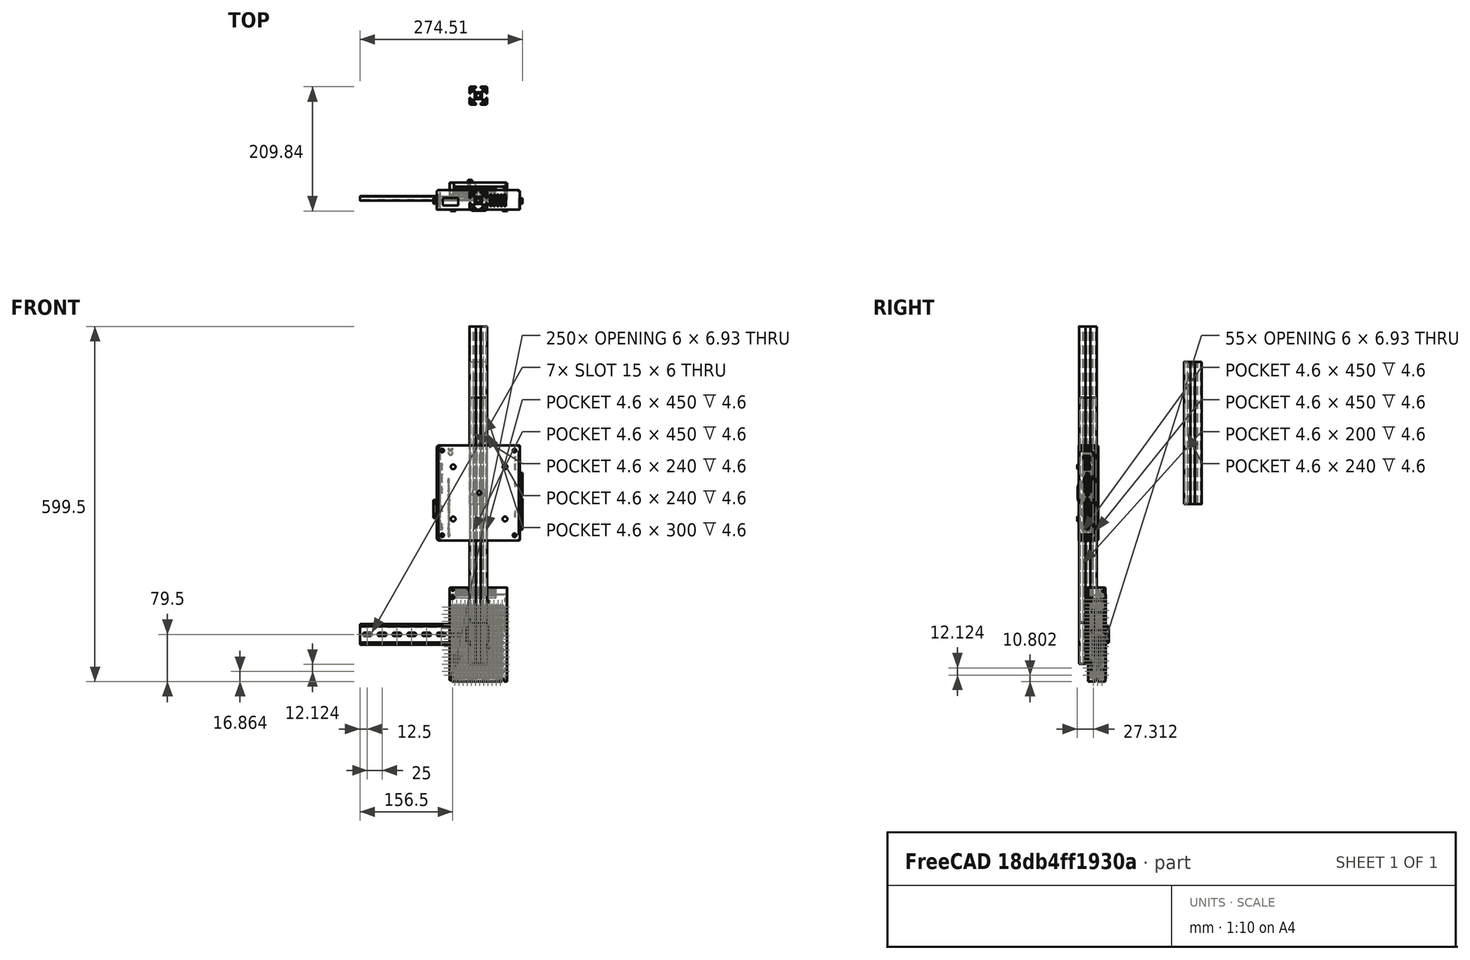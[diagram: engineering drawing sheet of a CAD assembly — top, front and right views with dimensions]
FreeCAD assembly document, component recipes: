
FREECAD ASSEMBLY — COMPONENT RECIPES ("electronics-box")

This assembly document has 40 components, labeled P0..P39 below (a component is one placed body or linked part). 7 of them carry a construction recipe — the FreeCAD feature program that regenerates the part from scratch, quoted from this document or its linked companion documents; the rest are supplied as boundary geometry only. No exploded tour is included for this assembly.
COMPONENT P0 — geometry summary ("LRS-155"; no construction recipe available for this part):
  bounding box: 159.0 x 97.0 x 30.0 mm
  tessellated surface: 57,942 triangles
  volume: 73054 mm^3 (16% of its bounding box)
COMPONENT P1 — geometry summary ("LRS-156"; no construction recipe available for this part):
  bounding box: 159.0 x 97.0 x 30.0 mm
  tessellated surface: 57,942 triangles
  volume: 73054 mm^3 (16% of its bounding box)
COMPONENT P2 — geometry summary ("SMC100CC001"; no construction recipe available for this part):
  bounding box: 161.0 x 150.5 x 35.3 mm
  tessellated surface: 51,434 triangles
  volume: 736162 mm^3 (86% of its bounding box)
COMPONENT P3 — geometry summary ("SMC100CC002"; no construction recipe available for this part):
  bounding box: 161.0 x 150.5 x 35.3 mm
  tessellated surface: 51,434 triangles
  volume: 736162 mm^3 (86% of its bounding box)
COMPONENT P4 — geometry summary ("3030-angle-bracket-001"; no construction recipe available for this part):
  bounding box: 36.7 x 36.7 x 28.0 mm
  tessellated surface: 1,116 triangles
  volume: 10483 mm^3 (28% of its bounding box)
  symmetry: mirror-symmetric across its x mid-plane
COMPONENT P5 — geometry summary ("3030-angle-bracket-002"; no construction recipe available for this part):
  bounding box: 36.7 x 36.7 x 28.0 mm
  tessellated surface: 1,116 triangles
  volume: 10483 mm^3 (28% of its bounding box)
  symmetry: mirror-symmetric across its x mid-plane
COMPONENT P6 — geometry summary ("3030-angle-bracket-003"; no construction recipe available for this part):
  bounding box: 36.7 x 36.7 x 28.0 mm
  tessellated surface: 1,116 triangles
  volume: 10483 mm^3 (28% of its bounding box)
  symmetry: mirror-symmetric across its x mid-plane
COMPONENT P7 — geometry summary ("3030-angle-bracket-004"; no construction recipe available for this part):
  bounding box: 36.7 x 36.7 x 28.0 mm
  tessellated surface: 1,116 triangles
  volume: 10483 mm^3 (28% of its bounding box)
  symmetry: mirror-symmetric across its x mid-plane
COMPONENT P8 — geometry summary ("3030-angle-bracket-005"; no construction recipe available for this part):
  bounding box: 36.7 x 36.7 x 28.0 mm
  tessellated surface: 1,116 triangles
  volume: 10483 mm^3 (28% of its bounding box)
  symmetry: mirror-symmetric across its x mid-plane
COMPONENT P9 — geometry summary ("3030-angle-bracket-006"; no construction recipe available for this part):
  bounding box: 36.7 x 36.7 x 28.0 mm
  tessellated surface: 1,116 triangles
  volume: 10483 mm^3 (28% of its bounding box)
  symmetry: mirror-symmetric across its x mid-plane
COMPONENT P10 — geometry summary ("3030-angle-bracket-007"; no construction recipe available for this part):
  bounding box: 36.7 x 36.7 x 28.0 mm
  tessellated surface: 1,116 triangles
  volume: 10483 mm^3 (28% of its bounding box)
  symmetry: mirror-symmetric across its x mid-plane
COMPONENT P11 — geometry summary ("3030-angle-bracket-008"; no construction recipe available for this part):
  bounding box: 36.7 x 36.7 x 28.0 mm
  tessellated surface: 1,116 triangles
  volume: 10483 mm^3 (28% of its bounding box)
  symmetry: mirror-symmetric across its x mid-plane
COMPONENT P12 — geometry summary ("3030-angle-bracket-009"; no construction recipe available for this part):
  bounding box: 36.7 x 36.7 x 28.0 mm
  tessellated surface: 1,116 triangles
  volume: 10483 mm^3 (28% of its bounding box)
  symmetry: mirror-symmetric across its x mid-plane
COMPONENT P13 — geometry summary ("3030-angle-bracket-010"; no construction recipe available for this part):
  bounding box: 36.7 x 36.7 x 28.0 mm
  tessellated surface: 1,116 triangles
  volume: 10483 mm^3 (28% of its bounding box)
  symmetry: mirror-symmetric across its x mid-plane
COMPONENT P14 — geometry summary ("3030-angle-bracket-011"; no construction recipe available for this part):
  bounding box: 36.7 x 36.7 x 28.0 mm
  tessellated surface: 1,116 triangles
  volume: 10483 mm^3 (28% of its bounding box)
  symmetry: mirror-symmetric across its x mid-plane
COMPONENT P15 — geometry summary ("3030-angle-bracket-012"; no construction recipe available for this part):
  bounding box: 36.7 x 36.7 x 28.0 mm
  tessellated surface: 1,116 triangles
  volume: 10483 mm^3 (28% of its bounding box)
  symmetry: mirror-symmetric across its x mid-plane
COMPONENT P16 — geometry summary ("3030-angle-bracket-013"; no construction recipe available for this part):
  bounding box: 36.7 x 36.7 x 28.0 mm
  tessellated surface: 1,116 triangles
  volume: 10483 mm^3 (28% of its bounding box)
  symmetry: mirror-symmetric across its x mid-plane
COMPONENT P17 — geometry summary ("3030-angle-bracket-014"; no construction recipe available for this part):
  bounding box: 36.7 x 36.7 x 28.0 mm
  tessellated surface: 1,116 triangles
  volume: 10483 mm^3 (28% of its bounding box)
  symmetry: mirror-symmetric across its x mid-plane
COMPONENT P18 — geometry summary ("3030-angle-bracket-015"; no construction recipe available for this part):
  bounding box: 36.7 x 36.7 x 28.0 mm
  tessellated surface: 1,116 triangles
  volume: 10483 mm^3 (28% of its bounding box)
  symmetry: mirror-symmetric across its x mid-plane
COMPONENT P19 — geometry summary ("3030-angle-bracket-016"; no construction recipe available for this part):
  bounding box: 36.7 x 36.7 x 28.0 mm
  tessellated surface: 1,116 triangles
  volume: 10483 mm^3 (28% of its bounding box)
  symmetry: mirror-symmetric across its x mid-plane
COMPONENT P20 — geometry summary ("3030-angle-bracket-017"; no construction recipe available for this part):
  bounding box: 36.7 x 36.7 x 28.0 mm
  tessellated surface: 1,116 triangles
  volume: 10483 mm^3 (28% of its bounding box)
  symmetry: mirror-symmetric across its x mid-plane
COMPONENT P21 — geometry summary ("3030-angle-bracket-018"; no construction recipe available for this part):
  bounding box: 36.7 x 36.7 x 28.0 mm
  tessellated surface: 1,116 triangles
  volume: 10483 mm^3 (28% of its bounding box)
  symmetry: mirror-symmetric across its x mid-plane
COMPONENT P22 — geometry summary ("alu-prof-3030-200-001"; no construction recipe available for this part):
  bounding box: 200.0 x 30.0 x 30.0 mm
  tessellated surface: 1,632 triangles
  volume: 62294 mm^3 (35% of its bounding box)
  symmetry: 2-fold rotationally symmetric about the x axis; 4-fold rotationally symmetric about the y axis; 2-fold rotationally symmetric about the z axis; mirror-symmetric across its x mid-plane, y mid-plane, z mid-plane
COMPONENT P23 — geometry summary ("alu-prof-3030-200-002"; no construction recipe available for this part):
  bounding box: 200.0 x 30.0 x 30.0 mm
  tessellated surface: 1,632 triangles
  volume: 62294 mm^3 (35% of its bounding box)
  symmetry: 2-fold rotationally symmetric about the x axis; 4-fold rotationally symmetric about the y axis; 2-fold rotationally symmetric about the z axis; mirror-symmetric across its x mid-plane, y mid-plane, z mid-plane
COMPONENT P24 — geometry summary ("alu-prof-3030-200-003"; no construction recipe available for this part):
  bounding box: 200.0 x 30.0 x 30.0 mm
  tessellated surface: 1,632 triangles
  volume: 62294 mm^3 (35% of its bounding box)
  symmetry: 2-fold rotationally symmetric about the x axis; 4-fold rotationally symmetric about the y axis; 2-fold rotationally symmetric about the z axis; mirror-symmetric across its x mid-plane, y mid-plane, z mid-plane
COMPONENT P25 — geometry summary ("alu-prof-3030-200-004"; no construction recipe available for this part):
  bounding box: 200.0 x 30.0 x 30.0 mm
  tessellated surface: 1,632 triangles
  volume: 62294 mm^3 (35% of its bounding box)
  symmetry: 2-fold rotationally symmetric about the x axis; 4-fold rotationally symmetric about the y axis; 2-fold rotationally symmetric about the z axis; mirror-symmetric across its x mid-plane, y mid-plane, z mid-plane
COMPONENT P26 — geometry summary ("alu-prof-3030-300-001"; no construction recipe available for this part):
  bounding box: 300.0 x 30.0 x 30.0 mm
  tessellated surface: 1,632 triangles
  volume: 93441 mm^3 (35% of its bounding box)
  symmetry: 2-fold rotationally symmetric about the x axis; 2-fold rotationally symmetric about the y axis; 4-fold rotationally symmetric about the z axis; mirror-symmetric across its x mid-plane, y mid-plane, z mid-plane
COMPONENT P27 — geometry summary ("alu-prof-3030-300-002"; no construction recipe available for this part):
  bounding box: 300.0 x 30.0 x 30.0 mm
  tessellated surface: 1,632 triangles
  volume: 93441 mm^3 (35% of its bounding box)
  symmetry: 2-fold rotationally symmetric about the x axis; 2-fold rotationally symmetric about the y axis; 4-fold rotationally symmetric about the z axis; mirror-symmetric across its x mid-plane, y mid-plane, z mid-plane
COMPONENT P28 — geometry summary ("alu-prof-3030-450-001"; no construction recipe available for this part):
  bounding box: 450.0 x 30.0 x 30.0 mm
  tessellated surface: 1,632 triangles
  volume: 140161 mm^3 (35% of its bounding box)
  symmetry: 4-fold rotationally symmetric about the x axis; 2-fold rotationally symmetric about the y axis; 2-fold rotationally symmetric about the z axis; mirror-symmetric across its x mid-plane, y mid-plane, z mid-plane
COMPONENT P29 — geometry summary ("alu-prof-3030-450-004"; no construction recipe available for this part):
  bounding box: 450.0 x 30.0 x 30.0 mm
  tessellated surface: 1,632 triangles
  volume: 140161 mm^3 (35% of its bounding box)
  symmetry: 4-fold rotationally symmetric about the x axis; 2-fold rotationally symmetric about the y axis; 2-fold rotationally symmetric about the z axis; mirror-symmetric across its x mid-plane, y mid-plane, z mid-plane
COMPONENT P30 — geometry summary ("alu-prof-3030-450-005"; no construction recipe available for this part):
  bounding box: 450.0 x 30.0 x 30.0 mm
  tessellated surface: 1,632 triangles
  volume: 140161 mm^3 (35% of its bounding box)
  symmetry: 4-fold rotationally symmetric about the x axis; 2-fold rotationally symmetric about the y axis; 2-fold rotationally symmetric about the z axis; mirror-symmetric across its x mid-plane, y mid-plane, z mid-plane
COMPONENT P31 — recipe-attached ("din_mount_part", a linked part whose construction recipe lives in a companion FreeCAD document of the same project; that document's serialized recipe follows).
Construction recipe (the companion document, serialized — sketch geometry with constraints, then the solid features built on it; lengths are millimeters unless a unit is written):

FCSTD DOCUMENT  (FreeCAD 1.0R39285 (Git))
Label: din_mount
License: All rights reserved
objects: Sketcher::SketchObject×4, PartDesign::Pad×2, PartDesign::Pocket×2, PartDesign::Chamfer×1, PartDesign::Body×1, App::Part×1
note: 24 computed .brp shape members not serialized (recipe doc carries the construction recipe); baked Part::Feature solids carry a one-line shape summary decoded from their .brp

FEATURE [Sketcher::SketchObject] Sketch
  ArcFitTolerance = 1e-06
  AttachmentSupport = -> [XY_Plane]
  FullyConstrained = true
  MakeInternals = false
  MapMode = 5
  expr: Constraints[33] = 10
  sketch-geometry (17):
    g0: LineSegment StartX=-17.9289 StartY=-15 StartZ=0 EndX=17.9289 EndY=-15 EndZ=0
    g1: LineSegment StartX=25 StartY=-7.92893 StartZ=0 EndX=25 EndY=7.92893 EndZ=0
    g2: LineSegment StartX=17.9289 StartY=15 StartZ=0 EndX=-17.9289 EndY=15 EndZ=0
    g3: LineSegment StartX=-25 StartY=7.92893 StartZ=0 EndX=-25 EndY=-7.92893 EndZ=0
    g4: GeomPoint [constr] X=0 Y=0 Z=0
    g5: ArcOfCircle [constr] CenterX=-17.9289 CenterY=7.92893 CenterZ=0 NormalX=0 NormalY=0 NormalZ=1 AngleXU=0 Radius=7.07107 StartAngle=1.5708 EndAngle=3.14159
    g6: GeomPoint [constr] X=-25 Y=15 Z=0
    g7: LineSegment StartX=-17.9289 StartY=15 StartZ=0 EndX=-25 EndY=7.92893 EndZ=0
    g8: ArcOfCircle [constr] CenterX=17.9289 CenterY=7.92893 CenterZ=0 NormalX=0 NormalY=0 NormalZ=1 AngleXU=0 Radius=7.07107 StartAngle=1e-16 EndAngle=1.5708
    g9: GeomPoint [constr] X=25 Y=15 Z=0
    g10: LineSegment StartX=25 StartY=7.92893 StartZ=0 EndX=17.9289 EndY=15 EndZ=0
    g11: ArcOfCircle [constr] CenterX=17.9289 CenterY=-7.92893 CenterZ=0 NormalX=0 NormalY=0 NormalZ=1 AngleXU=0 Radius=7.07107 StartAngle=4.71239 EndAngle=6.28319
    g12: GeomPoint [constr] X=25 Y=-15 Z=0
    g13: LineSegment StartX=17.9289 StartY=-15 StartZ=0 EndX=25 EndY=-7.92893 EndZ=0
    g14: ArcOfCircle [constr] CenterX=-17.9289 CenterY=-7.92893 CenterZ=0 NormalX=0 NormalY=0 NormalZ=1 AngleXU=0 Radius=7.07107 StartAngle=3.14159 EndAngle=4.71239
    g15: GeomPoint [constr] X=-25 Y=-15 Z=0
    g16: LineSegment StartX=-25 StartY=-7.92893 StartZ=0 EndX=-17.9289 EndY=-15 EndZ=0
  constraints (36):
    c: Horizontal(g0)
    c: Horizontal(g2)
    c: Vertical(g1)
    c: Vertical(g3)
    c: Symmetric(g9,g15,g4)
    c: Distance(g12,g15) = 50
    c: Distance(g15,g6) = 30
    c: Coincident(g4,g-1)
    c: PointOnObject(g6,g2)
    c: PointOnObject(g6,g3)
    c: Tangent(g2,g5) = -1.5708
    c: Tangent(g3,g5) = -1.5708
    c: Coincident(g7,g2)
    c: Coincident(g7,g3)
    c: PointOnObject(g9,g2)
    c: PointOnObject(g9,g1)
    c: Tangent(g2,g8) = -1.5708
    c: Tangent(g1,g8) = -1.5708
    c: Coincident(g10,g2)
    c: Coincident(g10,g1)
    c: PointOnObject(g12,g0)
    c: PointOnObject(g12,g1)
    c: Tangent(g0,g11) = -1.5708
    c: Tangent(g1,g11) = -1.5708
    c: Coincident(g13,g0)
    c: Coincident(g13,g1)
    c: PointOnObject(g15,g3)
    c: PointOnObject(g15,g0)
    c: Tangent(g3,g14) = -1.5708
    c: Tangent(g0,g14) = -1.5708
    c: Coincident(g16,g3)
    c: Coincident(g16,g0)
    c: Distance(g7,g7) = 10
    c: Distance(g10,g10) = 10
    c: Distance(g13,g13) = 10
    c: Distance(g16,g16) = 10
FEATURE [PartDesign::Pad] Pad
  Direction = (0,0,1)
  Length = 5
  Length2 = 10
  Profile = -> Sketch
  ReferenceAxis = -> Sketch [N_Axis]
  Refine = true
  Suppressed = false
  Type = 0
FEATURE [Sketcher::SketchObject] Sketch001
  ArcFitTolerance = 1e-06
  AttachmentSupport = -> [YZ_Plane]
  FullyConstrained = true
  MakeInternals = false
  MapMode = 5
  Placement = pos=(0,0,0) rot=(0.57735,0.57735,0.57735;2.0944rad)
  sketch-geometry (6):
    g0: LineSegment StartX=0 StartY=0 StartZ=0 EndX=-10 EndY=0 EndZ=0
    g1: LineSegment StartX=-10 StartY=0 StartZ=0 EndX=-10 EndY=15 EndZ=0
    g2: LineSegment StartX=0 StartY=0 StartZ=0 EndX=15 EndY=0 EndZ=0
    g3: LineSegment StartX=15 StartY=0 StartZ=0 EndX=15 EndY=60 EndZ=0
    g4: LineSegment StartX=15 StartY=60 StartZ=0 EndX=3 EndY=60 EndZ=0
    g5: LineSegment StartX=3 StartY=60 StartZ=0 EndX=-10 EndY=15 EndZ=0
  constraints (17):
    c: Distance(g0) = 10
    c: Coincident(g0,g-1)
    c: PointOnObject(g0,g-1)
    c: Distance(g1) = 15
    c: Coincident(g1,g0)
    c: Vertical(g1)
    c: Distance(g2) = 15
    c: Coincident(g2,g0)
    c: PointOnObject(g2,g-1)
    c: Distance(g3) = 60
    c: Coincident(g3,g2)
    c: Vertical(g3)
    c: Distance(g4) = 12
    c: Coincident(g4,g3)
    c: Horizontal(g4)
    c: Coincident(g5,g4)
    c: Coincident(g5,g1)
FEATURE [PartDesign::Pad] Pad001
  BaseFeature = -> Pad
  Direction = (1,0,0)
  Length = 15
  Length2 = 10
  Midplane = true
  Profile = -> Sketch001
  ReferenceAxis = -> Sketch001 [N_Axis]
  Refine = true
  Suppressed = false
  Type = 0
FEATURE [PartDesign::Chamfer] Chamfer
  Angle = 45
  Base = -> Pad001 [Edge37,Edge34,Edge29,Edge28,Edge33,Edge35,Edge30]
  BaseFeature = -> Pad001
  ChamferType = 0
  FlipDirection = false
  Refine = true
  Size = 2.5
  Size2 = 1
  SupportTransform = false
  Suppressed = false
  UseAllEdges = false
FEATURE [Sketcher::SketchObject] Sketch002
  ArcFitTolerance = 1e-06
  AttachmentSupport = -> [Chamfer]
  FullyConstrained = true
  MakeInternals = false
  MapMode = 5
  Placement = pos=(0,15,0) rot=(0,0.707107,0.707107;3.14159rad)
  sketch-geometry (2):
    g0: LineSegment [constr] StartX=0 StartY=0 StartZ=0 EndX=0 EndY=52.5 EndZ=0
    g1: Circle CenterX=0 CenterY=52.5 CenterZ=0 NormalX=0 NormalY=0 NormalZ=1 AngleXU=0 Radius=3.25
  constraints (5):
    c: Distance(g0) = 52.5
    c: Coincident(g0,g-1)
    c: Vertical(g0)
    c: Diameter(g1) = 6.5
    c: Coincident(g1,g0)
FEATURE [PartDesign::Pocket] Pocket
  BaseFeature = -> Chamfer
  Direction = (0,-1,2e-16)
  Length = 11
  Length2 = 5
  Profile = -> Sketch002
  ReferenceAxis = -> Sketch002 [N_Axis]
  Refine = true
  Suppressed = false
  Type = 0
FEATURE [Sketcher::SketchObject] Sketch003
  ArcFitTolerance = 1e-06
  AttachmentSupport = -> [Pocket]
  FullyConstrained = true
  MakeInternals = false
  MapMode = 5
  Placement = pos=(0,0,0) rot=(1,0,0;3.14159rad)
  sketch-geometry (4):
    g0: LineSegment [constr] StartX=0 StartY=0 StartZ=0 EndX=16 EndY=0 EndZ=0
    g1: LineSegment [constr] StartX=0 StartY=0 StartZ=0 EndX=-16 EndY=0 EndZ=0
    g2: Circle CenterX=-16 CenterY=0 CenterZ=0 NormalX=0 NormalY=0 NormalZ=1 AngleXU=0 Radius=2.6
    g3: Circle CenterX=16 CenterY=0 CenterZ=0 NormalX=0 NormalY=0 NormalZ=1 AngleXU=0 Radius=2.6
  constraints (10):
    c: Distance(g0) = 16
    c: Coincident(g0,g-1)
    c: PointOnObject(g0,g-1)
    c: Distance(g1) = 16
    c: Coincident(g1,g0)
    c: PointOnObject(g1,g-1)
    c: Diameter(g2) = 5.2
    c: Coincident(g2,g1)
    c: Diameter(g3) = 5.2
    c: Coincident(g3,g0)
FEATURE [PartDesign::Pocket] Pocket001
  BaseFeature = -> Pocket
  Direction = (0,0,1)
  Length = 5
  Length2 = 5
  Profile = -> Sketch003
  ReferenceAxis = -> Sketch003 [N_Axis]
  Refine = true
  Suppressed = false
  Type = 0
FEATURE [PartDesign::Body] Body  label="din_mount_body"
  AllowCompound = false
  Group = -> [Sketch,Pad,Sketch001,Pad001,Chamfer,Sketch002,Pocket,Sketch003,Pocket001]
  Origin = -> Origin
  Tip = -> Pocket001
FEATURE [App::Part] Part  label="din_mount_part"
  Group = -> [Body]
  Origin = -> Origin001
COMPONENT P32 — same part as P31; its construction recipe is shown at P31.
COMPONENT P33 — geometry summary ("din_rail_180mm001"; no construction recipe available for this part):
  bounding box: 180.0 x 35.0 x 7.5 mm
  tessellated surface: 2,968 triangles
  volume: 7678 mm^3 (16% of its bounding box)
  symmetry: mirror-symmetric across its z mid-plane
COMPONENT P34 — geometry summary ("dlp-power-supply-bracket-part"; no construction recipe available for this part):
  bounding box: 130.0 x 73.0 x 71.0 mm
  tessellated surface: 504 triangles
  volume: 33959 mm^3 (5% of its bounding box)
  symmetry: mirror-symmetric across its x mid-plane
COMPONENT P35 — recipe-attached ("ports-panel-part", a linked part whose construction recipe lives in a companion FreeCAD document of the same project; that document's serialized recipe follows).
Construction recipe (the companion document, serialized — sketch geometry with constraints, then the solid features built on it; lengths are millimeters unless a unit is written):

FCSTD DOCUMENT  (FreeCAD 1.0R39319 (Git))
Label: ports-panel
License: All rights reserved
objects: Sketcher::SketchObject×9, PartDesign::Pocket×7, PartDesign::Pad×2, PartDesign::Chamfer×2, PartDesign::Body×1, App::Part×1
note: 52 computed .brp shape members not serialized (recipe doc carries the construction recipe); baked Part::Feature solids carry a one-line shape summary decoded from their .brp

FEATURE [Sketcher::SketchObject] Sketch
  ArcFitTolerance = 1e-06
  AttachmentSupport = -> [XY_Plane]
  FullyConstrained = true
  MakeInternals = false
  MapMode = 5
  sketch-geometry (5):
    g0: LineSegment StartX=-115 StartY=-37.5 StartZ=0 EndX=115 EndY=-37.5 EndZ=0
    g1: LineSegment StartX=115 StartY=-37.5 StartZ=0 EndX=115 EndY=37.5 EndZ=0
    g2: LineSegment StartX=115 StartY=37.5 StartZ=0 EndX=-115 EndY=37.5 EndZ=0
    g3: LineSegment StartX=-115 StartY=37.5 StartZ=0 EndX=-115 EndY=-37.5 EndZ=0
    g4: GeomPoint [constr] X=0 Y=-1e-16 Z=0
  constraints (12):
    c: Coincident(g0,g1)
    c: Coincident(g1,g2)
    c: Coincident(g2,g3)
    c: Coincident(g3,g0)
    c: Horizontal(g0)
    c: Horizontal(g2)
    c: Vertical(g1)
    c: Vertical(g3)
    c: Symmetric(g2,g0,g4)
    c: Distance(g1,g3) = 230
    c: Distance(g0,g2) = 75
    c: Coincident(g4,g-1)
FEATURE [PartDesign::Pad] Pad
  Direction = (0,0,1)
  Length = 6.2
  Length2 = 10
  Profile = -> Sketch
  ReferenceAxis = -> Sketch [N_Axis]
  Refine = true
  Suppressed = false
  Type = 0
FEATURE [Sketcher::SketchObject] Sketch001
  ArcFitTolerance = 1e-06
  AttachmentSupport = -> [Pad]
  FullyConstrained = true
  MakeInternals = false
  MapMode = 5
  Placement = pos=(0,0,6.2) rot=(0,0,1;0rad)
  sketch-geometry (9):
    g0: LineSegment [constr] StartX=-115 StartY=-37.5 StartZ=0 EndX=115 EndY=-37.5 EndZ=0
    g1: LineSegment [constr] StartX=115 StartY=-37.5 StartZ=0 EndX=115 EndY=37.5 EndZ=0
    g2: LineSegment [constr] StartX=115 StartY=37.5 StartZ=0 EndX=-115 EndY=37.5 EndZ=0
    g3: LineSegment [constr] StartX=-115 StartY=37.5 StartZ=0 EndX=-115 EndY=-37.5 EndZ=0
    g4: GeomPoint [constr] X=0 Y=0 Z=0
    g5: LineSegment StartX=115 StartY=37.5 StartZ=0 EndX=-96 EndY=37.5 EndZ=0
    g6: LineSegment StartX=-96 StartY=37.5 StartZ=0 EndX=-96 EndY=33.5 EndZ=0
    g7: LineSegment StartX=-96 StartY=33.5 StartZ=0 EndX=115 EndY=33.5 EndZ=0
    g8: LineSegment StartX=115 StartY=33.5 StartZ=0 EndX=115 EndY=37.5 EndZ=0
  constraints (23):
    c: Coincident(g0,g1)
    c: Coincident(g1,g2)
    c: Coincident(g2,g3)
    c: Coincident(g3,g0)
    c: Horizontal(g0)
    c: Horizontal(g2)
    c: Vertical(g1)
    c: Vertical(g3)
    c: Symmetric(g2,g0,g4)
    c: Distance(g1,g3) = 230
    c: Distance(g0,g2) = 75
    c: Coincident(g4,g-1)
    c: Coincident(g5,g6)
    c: Coincident(g6,g7)
    c: Coincident(g7,g8)
    c: Coincident(g8,g5)
    c: Horizontal(g5)
    c: Horizontal(g7)
    c: Vertical(g6)
    c: Vertical(g8)
    c: Distance(g6,g8) = 211
    c: Distance(g5,g7) = 4
    c: Coincident(g5,g1)
FEATURE [PartDesign::Pocket] Pocket
  BaseFeature = -> Pad
  Direction = (0,0,-1)
  Length = 3.2
  Length2 = 5
  Profile = -> Sketch001
  ReferenceAxis = -> Sketch001 [N_Axis]
  Refine = true
  Suppressed = false
  Type = 0
FEATURE [PartDesign::Chamfer] Chamfer
  Angle = 45
  Base = -> Pocket [Edge6,Edge3,Edge8]
  BaseFeature = -> Pocket
  ChamferType = 0
  FlipDirection = false
  Refine = true
  Size = 2
  Size2 = 1
  SupportTransform = false
  Suppressed = false
  UseAllEdges = false
FEATURE [Sketcher::SketchObject] Sketch002
  ArcFitTolerance = 1e-06
  AttachmentSupport = -> [Chamfer]
  FullyConstrained = true
  MakeInternals = false
  MapMode = 5
  Placement = pos=(0,0,6.2) rot=(0,0,1;0rad)
  sketch-geometry (9):
    g0: LineSegment [constr] StartX=-100 StartY=-22.5 StartZ=0 EndX=100 EndY=-22.5 EndZ=0
    g1: LineSegment [constr] StartX=100 StartY=-22.5 StartZ=0 EndX=100 EndY=22.5 EndZ=0
    g2: LineSegment [constr] StartX=100 StartY=22.5 StartZ=0 EndX=-100 EndY=22.5 EndZ=0
    g3: LineSegment [constr] StartX=-100 StartY=22.5 StartZ=0 EndX=-100 EndY=-22.5 EndZ=0
    g4: GeomPoint [constr] X=0 Y=0 Z=0
    g5: Circle CenterX=-100 CenterY=-22.5 CenterZ=0 NormalX=0 NormalY=0 NormalZ=1 AngleXU=0 Radius=2.6
    g6: Circle CenterX=0 CenterY=-22.5 CenterZ=0 NormalX=0 NormalY=0 NormalZ=1 AngleXU=0 Radius=2.6
    g7: Circle CenterX=100 CenterY=-22.5 CenterZ=0 NormalX=0 NormalY=0 NormalZ=1 AngleXU=0 Radius=2.6
    g8: Circle CenterX=-100 CenterY=22.5 CenterZ=0 NormalX=0 NormalY=0 NormalZ=1 AngleXU=0 Radius=2.6
  constraints (20):
    c: Coincident(g0,g1)
    c: Coincident(g1,g2)
    c: Coincident(g2,g3)
    c: Coincident(g3,g0)
    c: Horizontal(g0)
    c: Horizontal(g2)
    c: Vertical(g1)
    c: Vertical(g3)
    c: Symmetric(g2,g0,g4)
    c: Distance(g1,g3) = 200
    c: Distance(g0,g2) = 45
    c: Coincident(g4,g-1)
    c: Diameter(g5) = 5.2
    c: Coincident(g5,g0)
    c: Diameter(g6) = 5.2
    c: Symmetric(g0,g0,g6)
    c: Diameter(g7) = 5.2
    c: Coincident(g7,g0)
    c: Diameter(g8) = 5.2
    c: Coincident(g8,g2)
FEATURE [PartDesign::Pocket] Pocket001
  BaseFeature = -> Chamfer
  Direction = (0,0,-1)
  Length = 10
  Length2 = 5
  Profile = -> Sketch002
  ReferenceAxis = -> Sketch002 [N_Axis]
  Refine = true
  Suppressed = false
  Type = 0
FEATURE [Sketcher::SketchObject] Sketch003
  ArcFitTolerance = 1e-06
  AttachmentSupport = -> [Pocket001]
  FullyConstrained = true
  MakeInternals = false
  MapMode = 5
  Placement = pos=(0,0,0) rot=(1,0,0;3.14159rad)
  sketch-geometry (17):
    g0: LineSegment [constr] StartX=-115 StartY=-37.5 StartZ=0 EndX=115 EndY=-37.5 EndZ=0
    g1: LineSegment [constr] StartX=115 StartY=-37.5 StartZ=0 EndX=115 EndY=37.5 EndZ=0
    g2: LineSegment [constr] StartX=115 StartY=37.5 StartZ=0 EndX=-115 EndY=37.5 EndZ=0
    g3: LineSegment [constr] StartX=-115 StartY=37.5 StartZ=0 EndX=-115 EndY=-37.5 EndZ=0
    g4: GeomPoint [constr] X=0 Y=0 Z=0
    g5: LineSegment [constr] StartX=115 StartY=37.5 StartZ=0 EndX=-115 EndY=37.5 EndZ=0
    g6: LineSegment [constr] StartX=-115 StartY=37.5 StartZ=0 EndX=-115 EndY=7.5 EndZ=0
    g7: LineSegment [constr] StartX=-115 StartY=7.5 StartZ=0 EndX=115 EndY=7.5 EndZ=0
    g8: LineSegment [constr] StartX=115 StartY=7.5 StartZ=0 EndX=115 EndY=37.5 EndZ=0
    g9: LineSegment [constr] StartX=0 StartY=0 StartZ=0 EndX=0 EndY=-1 EndZ=0
    g10: LineSegment [constr] StartX=0 StartY=-1 StartZ=0 EndX=20 EndY=-1 EndZ=0
    g11: LineSegment [constr] StartX=20 StartY=-1 StartZ=0 EndX=20 EndY=0 EndZ=0
    g12: LineSegment [constr] StartX=20 StartY=0 StartZ=0 EndX=0 EndY=0 EndZ=0
    g13: LineSegment StartX=20 StartY=-1 StartZ=0 EndX=20 EndY=-28.2 EndZ=0
    g14: LineSegment StartX=20 StartY=-28.2 StartZ=0 EndX=67.4 EndY=-28.2 EndZ=0
    g15: LineSegment StartX=67.4 StartY=-28.2 StartZ=0 EndX=67.4 EndY=-1 EndZ=0
    g16: LineSegment StartX=67.4 StartY=-1 StartZ=0 EndX=20 EndY=-1 EndZ=0
  constraints (45):
    c: Coincident(g0,g1)
    c: Coincident(g1,g2)
    c: Coincident(g2,g3)
    c: Coincident(g3,g0)
    c: Horizontal(g0)
    c: Horizontal(g2)
    c: Vertical(g1)
    c: Vertical(g3)
    c: Symmetric(g2,g0,g4)
    c: Distance(g1,g3) = 230
    c: Distance(g0,g2) = 75
    c: Coincident(g4,g-1)
    c: Coincident(g5,g6)
    c: Coincident(g6,g7)
    c: Coincident(g7,g8)
    c: Coincident(g8,g5)
    c: Horizontal(g5)
    c: Horizontal(g7)
    c: Vertical(g6)
    c: Vertical(g8)
    c: Distance(g5,g7) = 30
    c: Coincident(g5,g1)
    c: PointOnObject(g6,g3)
    c: Coincident(g9,g10)
    c: Coincident(g10,g11)
    c: Coincident(g11,g12)
    c: Coincident(g12,g9)
    c: Vertical(g9)
    c: Vertical(g11)
    c: Horizontal(g10)
    c: Horizontal(g12)
    c: Distance(g9,g11) = 20
    c: Distance(g10,g12) = 1
    c: Coincident(g9,g4)
    c: Coincident(g13,g14)
    c: Coincident(g14,g15)
    c: Coincident(g15,g16)
    c: Coincident(g16,g13)
    c: Vertical(g13)
    c: Vertical(g15)
    c: Horizontal(g14)
    c: Horizontal(g16)
    c: Distance(g13,g15) = 47.4
    c: Distance(g14,g16) = 27.2
    c: Coincident(g13,g10)
FEATURE [PartDesign::Pocket] Pocket002
  BaseFeature = -> Pocket001
  Direction = (0,0,1)
  Length = 7
  Length2 = 5
  Profile = -> Sketch003
  ReferenceAxis = -> Sketch003 [N_Axis]
  Refine = true
  Suppressed = false
  Type = 0
FEATURE [Sketcher::SketchObject] Sketch004
  ArcFitTolerance = 1e-06
  AttachmentSupport = -> [Pocket002]
  FullyConstrained = true
  MakeInternals = false
  MapMode = 5
  Placement = pos=(0,0,6.2) rot=(0,0,1;0rad)
  sketch-geometry (15):
    g0: LineSegment [constr] StartX=0 StartY=0 StartZ=0 EndX=30.7 EndY=0 EndZ=0
    g1: LineSegment [constr] StartX=30.7 StartY=0 StartZ=0 EndX=30.7 EndY=14.6 EndZ=0
    g2: LineSegment [constr] StartX=30.7 StartY=14.6 StartZ=0 EndX=0 EndY=14.6 EndZ=0
    g3: LineSegment [constr] StartX=0 StartY=14.6 StartZ=0 EndX=0 EndY=0 EndZ=0
    g4: LineSegment StartX=23.2 StartY=-0.4 StartZ=0 EndX=38.2 EndY=-0.4 EndZ=0
    g5: LineSegment StartX=38.2 StartY=-0.4 StartZ=0 EndX=38.2 EndY=29.6 EndZ=0
    g6: LineSegment StartX=38.2 StartY=29.6 StartZ=0 EndX=23.2 EndY=29.6 EndZ=0
    g7: LineSegment StartX=23.2 StartY=29.6 StartZ=0 EndX=23.2 EndY=-0.4 EndZ=0
    g8: GeomPoint [constr] X=30.7 Y=14.6 Z=0
    g9: LineSegment [constr] StartX=30.7 StartY=14.6 StartZ=0 EndX=56.7 EndY=14.6 EndZ=0
    g10: LineSegment StartX=49.2 StartY=-0.4 StartZ=0 EndX=64.2 EndY=-0.4 EndZ=0
    g11: LineSegment StartX=64.2 StartY=-0.4 StartZ=0 EndX=64.2 EndY=29.6 EndZ=0
    g12: LineSegment StartX=64.2 StartY=29.6 StartZ=0 EndX=49.2 EndY=29.6 EndZ=0
    g13: LineSegment StartX=49.2 StartY=29.6 StartZ=0 EndX=49.2 EndY=-0.4 EndZ=0
    g14: GeomPoint [constr] X=56.7 Y=14.6 Z=0
  constraints (38):
    c: Coincident(g0,g1)
    c: Coincident(g1,g2)
    c: Coincident(g2,g3)
    c: Coincident(g3,g0)
    c: Horizontal(g0)
    c: Horizontal(g2)
    c: Vertical(g1)
    c: Vertical(g3)
    c: Distance(g1,g3) = 30.7
    c: Distance(g0,g2) = 14.6
    c: Coincident(g0,g-1)
    c: Coincident(g4,g5)
    c: Coincident(g5,g6)
    c: Coincident(g6,g7)
    c: Coincident(g7,g4)
    c: Horizontal(g4)
    c: Horizontal(g6)
    c: Vertical(g5)
    c: Vertical(g7)
    c: Symmetric(g6,g4,g8)
    c: Distance(g5,g7) = 15
    c: Distance(g4,g6) = 30
    c: Coincident(g8,g1)
    c: Distance(g9) = 26
    c: Coincident(g9,g1)
    c: Horizontal(g9)
    c: Coincident(g10,g11)
    c: Coincident(g11,g12)
    c: Coincident(g12,g13)
    c: Coincident(g13,g10)
    c: Horizontal(g10)
    c: Horizontal(g12)
    c: Vertical(g11)
    c: Vertical(g13)
    c: Symmetric(g12,g10,g14)
    c: Distance(g11,g13) = 15
    c: Distance(g10,g12) = 30
    c: Coincident(g14,g9)
FEATURE [PartDesign::Pocket] Pocket003
  BaseFeature = -> Pocket002
  Direction = (0,0,-1)
  Length = 5.6
  Length2 = 5
  Profile = -> Sketch004
  ReferenceAxis = -> Sketch004 [N_Axis]
  Refine = true
  Suppressed = false
  Type = 0
FEATURE [Sketcher::SketchObject] Sketch005
  ArcFitTolerance = 1e-06
  AttachmentSupport = -> [Pocket003]
  FullyConstrained = true
  MakeInternals = false
  MapMode = 5
  Placement = pos=(0,0,6.2) rot=(0,0,1;0rad)
  sketch-geometry (18):
    g0: LineSegment [constr] StartX=-115 StartY=-37.5 StartZ=0 EndX=115 EndY=-37.5 EndZ=0
    g1: LineSegment [constr] StartX=115 StartY=-37.5 StartZ=0 EndX=115 EndY=37.5 EndZ=0
    g2: LineSegment [constr] StartX=115 StartY=37.5 StartZ=0 EndX=-115 EndY=37.5 EndZ=0
    g3: LineSegment [constr] StartX=-115 StartY=37.5 StartZ=0 EndX=-115 EndY=-37.5 EndZ=0
    g4: GeomPoint [constr] X=0 Y=0 Z=0
    g5: LineSegment [constr] StartX=115 StartY=-37.5 StartZ=0 EndX=115 EndY=-7.5 EndZ=0
    g6: LineSegment [constr] StartX=115 StartY=-7.5 StartZ=0 EndX=-115 EndY=-7.5 EndZ=0
    g7: LineSegment [constr] StartX=-115 StartY=-7.5 StartZ=0 EndX=-115 EndY=-37.5 EndZ=0
    g8: LineSegment [constr] StartX=-115 StartY=-37.5 StartZ=0 EndX=115 EndY=-37.5 EndZ=0
    g9: LineSegment [constr] StartX=0 StartY=0 StartZ=0 EndX=0 EndY=14.2 EndZ=0
    g10: LineSegment [constr] StartX=0 StartY=14.2 StartZ=0 EndX=-40 EndY=14.2 EndZ=0
    g11: LineSegment [constr] StartX=-40 StartY=14.2 StartZ=0 EndX=-40 EndY=0 EndZ=0
    g12: LineSegment [constr] StartX=-40 StartY=0 StartZ=0 EndX=0 EndY=0 EndZ=0
    g13: LineSegment StartX=-48 StartY=7.6 StartZ=0 EndX=-32 EndY=7.6 EndZ=0
    g14: LineSegment StartX=-32 StartY=7.6 StartZ=0 EndX=-32 EndY=20.8 EndZ=0
    g15: LineSegment StartX=-32 StartY=20.8 StartZ=0 EndX=-48 EndY=20.8 EndZ=0
    g16: LineSegment StartX=-48 StartY=20.8 StartZ=0 EndX=-48 EndY=7.6 EndZ=0
    g17: GeomPoint [constr] X=-40 Y=14.2 Z=0
  constraints (46):
    c: Coincident(g0,g1)
    c: Coincident(g1,g2)
    c: Coincident(g2,g3)
    c: Coincident(g3,g0)
    c: Horizontal(g0)
    c: Horizontal(g2)
    c: Vertical(g1)
    c: Vertical(g3)
    c: Symmetric(g2,g0,g4)
    c: Distance(g1,g3) = 230
    c: Distance(g0,g2) = 75
    c: Coincident(g4,g-1)
    c: Coincident(g5,g6)
    c: Coincident(g6,g7)
    c: Coincident(g7,g8)
    c: Coincident(g8,g5)
    c: Vertical(g5)
    c: Vertical(g7)
    c: Horizontal(g6)
    c: Horizontal(g8)
    c: Distance(g6,g8) = 30
    c: Coincident(g5,g0)
    c: PointOnObject(g6,g3)
    c: Coincident(g9,g10)
    c: Coincident(g10,g11)
    c: Coincident(g11,g12)
    c: Coincident(g12,g9)
    c: Vertical(g9)
    c: Vertical(g11)
    c: Horizontal(g10)
    c: Horizontal(g12)
    c: Distance(g9,g11) = 40
    c: Distance(g10,g12) = 14.2
    c: Coincident(g9,g4)
    c: Coincident(g13,g14)
    c: Coincident(g14,g15)
    c: Coincident(g15,g16)
    c: Coincident(g16,g13)
    c: Horizontal(g13)
    c: Horizontal(g15)
    c: Vertical(g14)
    c: Vertical(g16)
    c: Symmetric(g15,g13,g17)
    c: Distance(g14,g16) = 16
    c: Distance(g13,g15) = 13.2
    c: Coincident(g17,g10)
FEATURE [PartDesign::Pocket] Pocket004
  BaseFeature = -> Pocket003
  Direction = (0,0,-1)
  Length = 8
  Length2 = 5
  Profile = -> Sketch005
  ReferenceAxis = -> Sketch005 [N_Axis]
  Refine = true
  Suppressed = false
  Type = 0
FEATURE [Sketcher::SketchObject] Sketch006
  ArcFitTolerance = 1e-06
  AttachmentSupport = -> [Pocket004]
  FullyConstrained = true
  MakeInternals = false
  MapMode = 5
  Placement = pos=(0,0,6.2) rot=(0,0,1;0rad)
  sketch-geometry (9):
    g0: LineSegment [constr] StartX=0 StartY=0 StartZ=0 EndX=0 EndY=14.2 EndZ=0
    g1: LineSegment [constr] StartX=0 StartY=14.2 StartZ=0 EndX=-40 EndY=14.2 EndZ=0
    g2: LineSegment [constr] StartX=-40 StartY=14.2 StartZ=0 EndX=-40 EndY=0 EndZ=0
    g3: LineSegment [constr] StartX=-40 StartY=0 StartZ=0 EndX=0 EndY=0 EndZ=0
    g4: LineSegment StartX=-50.25 StartY=4.95 StartZ=0 EndX=-29.75 EndY=4.95 EndZ=0
    g5: LineSegment StartX=-29.75 StartY=4.95 StartZ=0 EndX=-29.75 EndY=23.45 EndZ=0
    g6: LineSegment StartX=-29.75 StartY=23.45 StartZ=0 EndX=-50.25 EndY=23.45 EndZ=0
    g7: LineSegment StartX=-50.25 StartY=23.45 StartZ=0 EndX=-50.25 EndY=4.95 EndZ=0
    g8: GeomPoint [constr] X=-40 Y=14.2 Z=0
  constraints (23):
    c: Coincident(g0,g1)
    c: Coincident(g1,g2)
    c: Coincident(g2,g3)
    c: Coincident(g3,g0)
    c: Vertical(g0)
    c: Vertical(g2)
    c: Horizontal(g1)
    c: Horizontal(g3)
    c: Distance(g0,g2) = 40
    c: Distance(g1,g3) = 14.2
    c: Coincident(g0,g-1)
    c: Coincident(g4,g5)
    c: Coincident(g5,g6)
    c: Coincident(g6,g7)
    c: Coincident(g7,g4)
    c: Horizontal(g4)
    c: Horizontal(g6)
    c: Vertical(g5)
    c: Vertical(g7)
    c: Symmetric(g6,g4,g8)
    c: Distance(g5,g7) = 20.5
    c: Distance(g4,g6) = 18.5
    c: Coincident(g8,g1)
FEATURE [PartDesign::Pocket] Pocket005
  BaseFeature = -> Pocket004
  Direction = (0,0,-1)
  Length = 5.6
  Length2 = 5
  Profile = -> Sketch006
  ReferenceAxis = -> Sketch006 [N_Axis]
  Refine = true
  Suppressed = false
  Type = 0
FEATURE [Sketcher::SketchObject] Sketch007
  ArcFitTolerance = 1e-06
  AttachmentSupport = -> [Pocket005]
  FullyConstrained = true
  MakeInternals = false
  MapMode = 5
  Placement = pos=(0,0,6.2) rot=(0,0,1;0rad)
  sketch-geometry (14):
    g0: LineSegment [constr] StartX=0 StartY=0 StartZ=0 EndX=0 EndY=14.2 EndZ=0
    g1: LineSegment [constr] StartX=0 StartY=14.2 StartZ=0 EndX=-40 EndY=14.2 EndZ=0
    g2: LineSegment [constr] StartX=-40 StartY=14.2 StartZ=0 EndX=-40 EndY=0 EndZ=0
    g3: LineSegment [constr] StartX=-40 StartY=0 StartZ=0 EndX=0 EndY=0 EndZ=0
    g4: LineSegment StartX=-50.25 StartY=4.95 StartZ=0 EndX=-29.75 EndY=4.95 EndZ=0
    g5: LineSegment StartX=-29.75 StartY=4.95 StartZ=0 EndX=-29.75 EndY=23.45 EndZ=0
    g6: LineSegment StartX=-29.75 StartY=23.45 StartZ=0 EndX=-50.25 EndY=23.45 EndZ=0
    g7: LineSegment StartX=-50.25 StartY=23.45 StartZ=0 EndX=-50.25 EndY=4.95 EndZ=0
    g8: GeomPoint [constr] X=-40 Y=14.2 Z=0
    g9: LineSegment StartX=-53.5 StartY=1.7 StartZ=0 EndX=-26.5 EndY=1.7 EndZ=0
    g10: LineSegment StartX=-26.5 StartY=1.7 StartZ=0 EndX=-26.5 EndY=26.7 EndZ=0
    g11: LineSegment StartX=-26.5 StartY=26.7 StartZ=0 EndX=-53.5 EndY=26.7 EndZ=0
    g12: LineSegment StartX=-53.5 StartY=26.7 StartZ=0 EndX=-53.5 EndY=1.7 EndZ=0
    g13: GeomPoint [constr] X=-40 Y=14.2 Z=0
  constraints (35):
    c: Coincident(g0,g1)
    c: Coincident(g1,g2)
    c: Coincident(g2,g3)
    c: Coincident(g3,g0)
    c: Vertical(g0)
    c: Vertical(g2)
    c: Horizontal(g1)
    c: Horizontal(g3)
    c: Distance(g0,g2) = 40
    c: Distance(g1,g3) = 14.2
    c: Coincident(g0,g-1)
    c: Coincident(g4,g5)
    c: Coincident(g5,g6)
    c: Coincident(g6,g7)
    c: Coincident(g7,g4)
    c: Horizontal(g4)
    c: Horizontal(g6)
    c: Vertical(g5)
    c: Vertical(g7)
    c: Symmetric(g6,g4,g8)
    c: Distance(g5,g7) = 20.5
    c: Distance(g4,g6) = 18.5
    c: Coincident(g8,g1)
    c: Coincident(g9,g10)
    c: Coincident(g10,g11)
    c: Coincident(g11,g12)
    c: Coincident(g12,g9)
    c: Horizontal(g9)
    c: Horizontal(g11)
    c: Vertical(g10)
    c: Vertical(g12)
    c: Symmetric(g11,g9,g13)
    c: Distance(g10,g12) = 27
    c: Distance(g9,g11) = 25
    c: Coincident(g13,g1)
FEATURE [PartDesign::Pad] Pad001
  BaseFeature = -> Pocket005
  Direction = (0,0,1)
  Length = 20
  Length2 = 10
  Profile = -> Sketch007
  ReferenceAxis = -> Sketch007 [N_Axis]
  Refine = true
  Suppressed = false
  Type = 0
FEATURE [PartDesign::Chamfer] Chamfer001
  Angle = 45
  Base = -> Pad001 [Edge72,Edge73,Edge77,Edge75]
  BaseFeature = -> Pad001
  ChamferType = 0
  FlipDirection = false
  Refine = true
  Size = 3
  Size2 = 1
  SupportTransform = false
  Suppressed = false
  UseAllEdges = false
FEATURE [Sketcher::SketchObject] Sketch008
  ArcFitTolerance = 1e-06
  AttachmentSupport = -> [Chamfer001]
  FullyConstrained = true
  MakeInternals = false
  MapMode = 5
  Placement = pos=(-53.5,0,0) rot=(0.57735,-0.57735,-0.57735;2.0944rad)
  sketch-geometry (9):
    g0: LineSegment [constr] StartX=0 StartY=0 StartZ=0 EndX=0 EndY=6.2 EndZ=0
    g1: LineSegment [constr] StartX=0 StartY=6.2 StartZ=0 EndX=-26.7 EndY=6.2 EndZ=0
    g2: LineSegment [constr] StartX=-26.7 StartY=6.2 StartZ=0 EndX=-26.7 EndY=0 EndZ=0
    g3: LineSegment [constr] StartX=-26.7 StartY=0 StartZ=0 EndX=0 EndY=0 EndZ=0
    g4: LineSegment [constr] StartX=-26.7 StartY=6.2 StartZ=0 EndX=-14.2 EndY=6.2 EndZ=0
    g5: LineSegment [constr] StartX=-14.2 StartY=6.2 StartZ=0 EndX=-14.2 EndY=16.2 EndZ=0
    g6: LineSegment [constr] StartX=-14.2 StartY=16.2 StartZ=0 EndX=-26.7 EndY=16.2 EndZ=0
    g7: LineSegment [constr] StartX=-26.7 StartY=16.2 StartZ=0 EndX=-26.7 EndY=6.2 EndZ=0
    g8: Circle CenterX=-14.2 CenterY=16.2 CenterZ=0 NormalX=0 NormalY=0 NormalZ=1 AngleXU=0 Radius=1.25
  constraints (24):
    c: Coincident(g0,g1)
    c: Coincident(g1,g2)
    c: Coincident(g2,g3)
    c: Coincident(g3,g0)
    c: Vertical(g0)
    c: Vertical(g2)
    c: Horizontal(g1)
    c: Horizontal(g3)
    c: Distance(g0,g2) = 26.7
    c: Distance(g1,g3) = 6.2
    c: Coincident(g0,g-1)
    c: Coincident(g4,g5)
    c: Coincident(g5,g6)
    c: Coincident(g6,g7)
    c: Coincident(g7,g4)
    c: Horizontal(g4)
    c: Horizontal(g6)
    c: Vertical(g5)
    c: Vertical(g7)
    c: Distance(g5,g7) = 12.5
    c: Distance(g4,g6) = 10
    c: Coincident(g4,g1)
    c: Diameter(g8) = 2.5
    c: Coincident(g8,g5)
FEATURE [PartDesign::Pocket] Pocket006
  BaseFeature = -> Chamfer001
  Direction = (1,0,0)
  Length = 30
  Length2 = 5
  Profile = -> Sketch008
  ReferenceAxis = -> Sketch008 [N_Axis]
  Refine = true
  Suppressed = false
  Type = 0
FEATURE [PartDesign::Body] Body  label="ports-panel-body"
  AllowCompound = false
  Group = -> [Sketch,Pad,Sketch001,Pocket,Chamfer,Sketch002,Pocket001,Sketch003,Pocket002,Sketch004,Pocket003,Sketch005,Pocket004,Sketch006,Pocket005,Sketch007,Pad001,Chamfer001,Sketch008,Pocket006]
  Origin = -> Origin
  Tip = -> Pocket006
FEATURE [App::Part] Part  label="ports-panel-part"
  Group = -> [Body]
  Origin = -> Origin001
COMPONENT P36 — recipe-attached ("power-supply-bracket-part", a linked part whose construction recipe lives in a companion FreeCAD document of the same project; that document's serialized recipe follows).
Construction recipe (the companion document, serialized — sketch geometry with constraints, then the solid features built on it; lengths are millimeters unless a unit is written):

FCSTD DOCUMENT  (FreeCAD 1.0R39285 (Git))
Label: power-supply-bracket
License: All rights reserved
LicenseURL: https://en.wikipedia.org/wiki/All_rights_reserved
objects: Sketcher::SketchObject×9, PartDesign::Pad×5, PartDesign::Chamfer×4, PartDesign::Hole×2, PartDesign::Fillet×1, PartDesign::Body×1, App::Part×1
note: 55 computed .brp shape members not serialized (recipe doc carries the construction recipe); baked Part::Feature solids carry a one-line shape summary decoded from their .brp

FEATURE [Sketcher::SketchObject] Sketch
  ArcFitTolerance = 1e-06
  AttachmentSupport = -> [XY_Plane]
  FullyConstrained = true
  MakeInternals = false
  MapMode = 5
  sketch-geometry (106):
    g0: LineSegment [constr] StartX=0 StartY=0 StartZ=0 EndX=30 EndY=0 EndZ=0
    g1: LineSegment StartX=30 StartY=0 StartZ=0 EndX=30 EndY=30 EndZ=0
    g2: LineSegment StartX=30 StartY=30 StartZ=0 EndX=0 EndY=30 EndZ=0
    g3: LineSegment [constr] StartX=0 StartY=30 StartZ=0 EndX=0 EndY=0 EndZ=0
    g4: LineSegment StartX=0 StartY=30 StartZ=0 EndX=0 EndY=34 EndZ=0
    g5: LineSegment [constr] StartX=0 StartY=34 StartZ=0 EndX=34 EndY=34 EndZ=0
    g6: LineSegment [constr] StartX=34 StartY=34 StartZ=0 EndX=34 EndY=0 EndZ=0
    g7: LineSegment [constr] StartX=34 StartY=0 StartZ=0 EndX=30 EndY=0 EndZ=0
    g8: LineSegment [constr] StartX=34 StartY=34 StartZ=0 EndX=34 EndY=64 EndZ=0
    g9: LineSegment StartX=0 StartY=34 StartZ=0 EndX=34 EndY=64 EndZ=0
    g10: LineSegment [constr] StartX=34 StartY=64 StartZ=0 EndX=34 EndY=-33 EndZ=0
    g11: LineSegment [constr] StartX=34 StartY=-33 StartZ=0 EndX=199 EndY=-33 EndZ=0
    g12: LineSegment StartX=199 StartY=-33 StartZ=0 EndX=199 EndY=64 EndZ=0
    g13: LineSegment StartX=199 StartY=64 StartZ=0 EndX=34 EndY=64 EndZ=0
    g14: LineSegment [constr] StartX=34 StartY=64 StartZ=0 EndX=34 EndY=58.5 EndZ=0
    g15: LineSegment [constr] StartX=44.5 StartY=64 StartZ=0 EndX=34 EndY=64 EndZ=0
    g16: LineSegment [constr] StartX=199 StartY=-33 StartZ=0 EndX=199 EndY=-26.5 EndZ=0
    g17: LineSegment [constr] StartX=199 StartY=-26.5 StartZ=0 EndX=196 EndY=-26.5 EndZ=0
    g18: LineSegment [constr] StartX=196 StartY=-26.5 StartZ=0 EndX=196 EndY=-33 EndZ=0
    g19: LineSegment [constr] StartX=196 StartY=-33 StartZ=0 EndX=199 EndY=-33 EndZ=0
    g20: LineSegment [constr] StartX=199 StartY=64 StartZ=0 EndX=40 EndY=64 EndZ=0
    g21: LineSegment [constr] StartX=40 StartY=64 StartZ=0 EndX=40 EndY=-33 EndZ=0
    g22: LineSegment [constr] StartX=40 StartY=-33 StartZ=0 EndX=199 EndY=-33 EndZ=0
    g23: LineSegment [constr] StartX=199 StartY=-33 StartZ=0 EndX=199 EndY=64 EndZ=0
    g24: LineSegment [constr] StartX=40 StartY=64 StartZ=0 EndX=40 EndY=58.5 EndZ=0
    g25: LineSegment [constr] StartX=40 StartY=58.5 StartZ=0 EndX=44.5 EndY=58.5 EndZ=0
    g26: LineSegment [constr] StartX=44.5 StartY=58.5 StartZ=0 EndX=44.5 EndY=64 EndZ=0
    g27: LineSegment [constr] StartX=44.5 StartY=64 StartZ=0 EndX=40 EndY=64 EndZ=0
    g28: LineSegment [constr] StartX=34 StartY=-33 StartZ=0 EndX=30 EndY=-33 EndZ=0
    g29: LineSegment StartX=30 StartY=0 StartZ=0 EndX=30 EndY=-33 EndZ=0
    g30: LineSegment StartX=30 StartY=-33 StartZ=0 EndX=30 EndY=-37 EndZ=0
    g31: LineSegment StartX=30 StartY=-37 StartZ=0 EndX=199 EndY=-37 EndZ=0
    g32: LineSegment StartX=199 StartY=-37 StartZ=0 EndX=199 EndY=-33 EndZ=0
    g33: LineSegment [constr] StartX=34 StartY=64 StartZ=0 EndX=34 EndY=49 EndZ=0
    g34: LineSegment [constr] StartX=34 StartY=49 StartZ=0 EndX=49 EndY=49 EndZ=0
    g35: LineSegment [constr] StartX=49 StartY=49 StartZ=0 EndX=49 EndY=64 EndZ=0
    g36: LineSegment [constr] StartX=49 StartY=64 StartZ=0 EndX=34 EndY=64 EndZ=0
    g37: LineSegment [constr] StartX=199 StartY=64 StartZ=0 EndX=184 EndY=64 EndZ=0
    g38: LineSegment [constr] StartX=184 StartY=64 StartZ=0 EndX=184 EndY=49 EndZ=0
    g39: LineSegment [constr] StartX=184 StartY=49 StartZ=0 EndX=199 EndY=49 EndZ=0
    g40: LineSegment [constr] StartX=199 StartY=49 StartZ=0 EndX=199 EndY=64 EndZ=0
    g41: LineSegment [constr] StartX=34 StartY=-33 StartZ=0 EndX=49 EndY=-33 EndZ=0
    g42: LineSegment [constr] StartX=49 StartY=-33 StartZ=0 EndX=49 EndY=-18 EndZ=0
    g43: LineSegment [constr] StartX=49 StartY=-18 StartZ=0 EndX=34 EndY=-18 EndZ=0
    g44: LineSegment [constr] StartX=34 StartY=-18 StartZ=0 EndX=34 EndY=-33 EndZ=0
    g45: LineSegment [constr] StartX=199 StartY=-33 StartZ=0 EndX=199 EndY=-18 EndZ=0
    g46: LineSegment [constr] StartX=199 StartY=-18 StartZ=0 EndX=184 EndY=-18 EndZ=0
    g47: LineSegment [constr] StartX=184 StartY=-18 StartZ=0 EndX=184 EndY=-33 EndZ=0
    g48: LineSegment [constr] StartX=184 StartY=-33 StartZ=0 EndX=199 EndY=-33 EndZ=0
    g49: LineSegment [constr] StartX=49 StartY=49 StartZ=0 EndX=184 EndY=-18 EndZ=0
    g50: LineSegment [constr] StartX=49 StartY=-18 StartZ=0 EndX=184 EndY=49 EndZ=0
    g51: LineSegment [constr] StartX=109 StartY=8 StartZ=0 EndX=124 EndY=8 EndZ=0
    g52: LineSegment [constr] StartX=124 StartY=8 StartZ=0 EndX=124 EndY=23 EndZ=0
    g53: LineSegment [constr] StartX=124 StartY=23 StartZ=0 EndX=109 EndY=23 EndZ=0
    g54: LineSegment [constr] StartX=109 StartY=23 StartZ=0 EndX=109 EndY=8 EndZ=0
    g55: GeomPoint [constr] X=116.5 Y=15.5 Z=0
    g56: LineSegment [constr] StartX=49 StartY=49 StartZ=0 EndX=184 EndY=49 EndZ=0
    g57: LineSegment [constr] StartX=184 StartY=49 StartZ=0 EndX=184 EndY=-18 EndZ=0
    g58: LineSegment [constr] StartX=184 StartY=-18 StartZ=0 EndX=49 EndY=-18 EndZ=0
    g59: LineSegment [constr] StartX=49 StartY=-18 StartZ=0 EndX=49 EndY=49 EndZ=0
    g60: LineSegment [constr] StartX=116.5 StartY=23 StartZ=0 EndX=49 EndY=56.5 EndZ=0
    g61: LineSegment [constr] StartX=116.5 StartY=23 StartZ=0 EndX=184 EndY=56.5 EndZ=0
    g62: LineSegment [constr] StartX=116.5 StartY=8 StartZ=0 EndX=49 EndY=-25.5 EndZ=0
    g63: LineSegment [constr] StartX=116.5 StartY=8 StartZ=0 EndX=184 EndY=-25.5 EndZ=0
    g64: LineSegment [constr] StartX=49 StartY=49 StartZ=0 EndX=64 EndY=49 EndZ=0
    g65: LineSegment [constr] StartX=49 StartY=-18 StartZ=0 EndX=64 EndY=-18 EndZ=0
    g66: LineSegment [constr] StartX=184 StartY=-18 StartZ=0 EndX=169 EndY=-18 EndZ=0
    g67: LineSegment [constr] StartX=184 StartY=49 StartZ=0 EndX=169 EndY=49 EndZ=0
    g68: LineSegment StartX=64 StartY=49 StartZ=0 EndX=116.5 EndY=23 EndZ=0
    g69: LineSegment StartX=169 StartY=49 StartZ=0 EndX=116.5 EndY=23 EndZ=0
    g70: LineSegment [constr] StartX=49 StartY=49 StartZ=0 EndX=116.5 EndY=15.5 EndZ=0
    g71: LineSegment [constr] StartX=116.5 StartY=15.5 StartZ=0 EndX=49 EndY=-18 EndZ=0
    g72: LineSegment [constr] StartX=49 StartY=49 StartZ=0 EndX=49 EndY=41.5 EndZ=0
    g73: LineSegment [constr] StartX=116.5 StartY=8 StartZ=0 EndX=49 EndY=41.5 EndZ=0
    g74: LineSegment [constr] StartX=184 StartY=49 StartZ=0 EndX=184 EndY=41.5 EndZ=0
    g75: LineSegment [constr] StartX=184 StartY=41.5 StartZ=0 EndX=116.5 EndY=8 EndZ=0
    g76: LineSegment [constr] StartX=49 StartY=-18 StartZ=0 EndX=49 EndY=-10.5 EndZ=0
    g77: LineSegment [constr] StartX=184 StartY=-18 StartZ=0 EndX=184 EndY=-10.5 EndZ=0
    g78: LineSegment [constr] StartX=184 StartY=-10.5 StartZ=0 EndX=116.5 EndY=23 EndZ=0
    g79: LineSegment [constr] StartX=116.5 StartY=23 StartZ=0 EndX=49 EndY=-10.5 EndZ=0
    g80: LineSegment StartX=64 StartY=49 StartZ=0 EndX=169 EndY=49 EndZ=0
    g81: LineSegment StartX=116.5 StartY=8 StartZ=0 EndX=64 EndY=-18 EndZ=0
    g82: LineSegment StartX=169 StartY=-18 StartZ=0 EndX=116.5 EndY=8 EndZ=0
    g83: LineSegment StartX=64 StartY=-18 StartZ=0 EndX=169 EndY=-18 EndZ=0
    g84: LineSegment [constr] StartX=116.5 StartY=15.5 StartZ=0 EndX=101.388 EndY=15.5 EndZ=0
    g85: LineSegment [constr] StartX=116.5 StartY=15.5 StartZ=0 EndX=131.612 EndY=15.5 EndZ=0
    g86: LineSegment StartX=49 StartY=41.5 StartZ=0 EndX=101.388 EndY=15.5 EndZ=0
    g87: LineSegment StartX=101.388 StartY=15.5 StartZ=0 EndX=49 EndY=-10.5 EndZ=0
    g88: LineSegment StartX=49 StartY=-10.5 StartZ=0 EndX=49 EndY=41.5 EndZ=0
    g89: LineSegment StartX=184 StartY=41.5 StartZ=0 EndX=131.612 EndY=15.5 EndZ=0
    g90: LineSegment StartX=131.612 StartY=15.5 StartZ=0 EndX=184 EndY=-10.5 EndZ=0
    g91: LineSegment StartX=184 StartY=-10.5 StartZ=0 EndX=184 EndY=41.5 EndZ=0
    g92: Circle [constr] CenterX=44.5 CenterY=58.5 CenterZ=0 NormalX=0 NormalY=0 NormalZ=1 AngleXU=0 Radius=1.75
    g93: Circle [constr] CenterX=196 CenterY=-26.5 CenterZ=0 NormalX=0 NormalY=0 NormalZ=1 AngleXU=0 Radius=1.75
    g94: LineSegment [constr] StartX=199 StartY=64 StartZ=0 EndX=194.5 EndY=64 EndZ=0
    g95: LineSegment [constr] StartX=194.5 StartY=64 StartZ=0 EndX=194.5 EndY=58.5 EndZ=0
    g96: LineSegment [constr] StartX=194.5 StartY=58.5 StartZ=0 EndX=199 EndY=58.5 EndZ=0
    g97: LineSegment [constr] StartX=199 StartY=58.5 StartZ=0 EndX=199 EndY=64 EndZ=0
    g98: Circle [constr] CenterX=194.5 CenterY=58.5 CenterZ=0 NormalX=0 NormalY=0 NormalZ=1 AngleXU=0 Radius=1.75
    g99: LineSegment [constr] StartX=194.5 StartY=58.5 StartZ=0 EndX=42 EndY=58.5 EndZ=0
    g100: LineSegment [constr] StartX=42 StartY=58.5 StartZ=0 EndX=42 EndY=-26.5 EndZ=0
    g101: Circle CenterX=42 CenterY=-26.5 CenterZ=0 NormalX=0 NormalY=0 NormalZ=1 AngleXU=0 Radius=1.75
    g102: ArcOfCircle CenterX=194.5 CenterY=58.5 CenterZ=0 NormalX=0 NormalY=0 NormalZ=1 AngleXU=0 Radius=1.75 StartAngle=4.71239 EndAngle=7.85398
    g103: ArcOfCircle CenterX=190.5 CenterY=58.5 CenterZ=0 NormalX=0 NormalY=0 NormalZ=1 AngleXU=0 Radius=1.75 StartAngle=1.5708 EndAngle=4.71239
    g104: LineSegment StartX=194.5 StartY=56.75 StartZ=0 EndX=190.5 EndY=56.75 EndZ=0
    g105: LineSegment StartX=194.5 StartY=60.25 StartZ=0 EndX=190.5 EndY=60.25 EndZ=0
  constraints (266):
    c: Coincident(g0,g1)
    c: Coincident(g1,g2)
    c: Coincident(g2,g3)
    c: Coincident(g3,g0)
    c: Horizontal(g0)
    c: Horizontal(g2)
    c: Vertical(g1)
    c: Vertical(g3)
    c: Distance(g1,g3) = 30
    c: Distance(g0,g2) = 30
    c: Coincident(g0,g-1)
    c: Distance(g4) = 4
    c: Coincident(g4,g2)
    c: PointOnObject(g4,g-2)
    c: Distance(g5) = 34
    c: Coincident(g5,g4)
    c: Horizontal(g5)
    c: Coincident(g6,g5)
    c: PointOnObject(g6,g-1)
    c: Vertical(g6)
    c: Coincident(g7,g6)
    c: Coincident(g7,g0)
    c: Distance(g8) = 30
    c: Coincident(g8,g5)
    c: Vertical(g8)
    c: Coincident(g9,g4)
    c: Coincident(g9,g8)
    c: Coincident(g10,g11)
    c: Coincident(g11,g12)
    c: Coincident(g12,g13)
    c: Coincident(g13,g10)
    c: Vertical(g10)
    c: Vertical(g12)
    c: Horizontal(g11)
    c: Horizontal(g13)
    c: Distance(g10,g12) = 165
    c: Distance(g11,g13) = 97
    c: Coincident(g10,g8)
    c: Coincident(g15,g14)
    c: Vertical(g14)
    c: Horizontal(g15)
    c: Distance(g14,g15) = 10.5
    c: Distance(g14,g15) = 5.5
    c: Coincident(g14,g8)
    c: Coincident(g16,g17)
    c: Coincident(g17,g18)
    c: Coincident(g18,g19)
    c: Coincident(g19,g16)
    c: Vertical(g16)
    c: Vertical(g18)
    c: Horizontal(g17)
    c: Horizontal(g19)
    c: Distance(g16,g18) = 3
    c: Distance(g17,g19) = 6.5
    c: Coincident(g16,g11)
    c: Coincident(g20,g21)
    c: Coincident(g21,g22)
    c: Coincident(g22,g23)
    c: Coincident(g23,g20)
    c: Horizontal(g20)
    c: Horizontal(g22)
    c: Vertical(g21)
    c: Vertical(g23)
    c: Distance(g21,g23) = 159
    c: Coincident(g20,g12)
    c: PointOnObject(g21,g11)
    c: Coincident(g24,g25)
    c: Coincident(g25,g26)
    c: Coincident(g26,g27)
    c: Coincident(g27,g24)
    c: Vertical(g24)
    c: Vertical(g26)
    c: Horizontal(g25)
    c: Horizontal(g27)
    c: Distance(g24,g26) = 4.5
    c: Distance(g25,g27) = 5.5
    c: Coincident(g24,g20)
    c: Distance(g28) = 4
    c: Coincident(g28,g10)
    c: Horizontal(g28)
    c: Coincident(g29,g0)
    c: Coincident(g29,g28)
    c: Distance(g30) = 4
    c: Coincident(g30,g28)
    c: Vertical(g30)
    c: Distance(g31) = 169
    c: Coincident(g31,g30)
    c: Horizontal(g31)
    c: Coincident(g32,g31)
    c: Coincident(g32,g11)
    c: Coincident(g33,g34)
    c: Coincident(g34,g35)
    c: Coincident(g35,g36)
    c: Coincident(g36,g33)
    c: Vertical(g33)
    c: Vertical(g35)
    c: Horizontal(g34)
    c: Horizontal(g36)
    c: Distance(g33,g35) = 15
    c: Distance(g34,g36) = 15
    c: Coincident(g33,g8)
    c: Coincident(g37,g38)
    c: Coincident(g38,g39)
    c: Coincident(g39,g40)
    c: Coincident(g40,g37)
    c: Horizontal(g37)
    c: Horizontal(g39)
    c: Vertical(g38)
    c: Vertical(g40)
    c: Distance(g38,g40) = 15
    c: Distance(g37,g39) = 15
    c: Coincident(g37,g12)
    c: Coincident(g41,g42)
    c: Coincident(g42,g43)
    c: Coincident(g43,g44)
    c: Coincident(g44,g41)
    c: Horizontal(g41)
    c: Horizontal(g43)
    c: Vertical(g42)
    c: Vertical(g44)
    c: Distance(g42,g44) = 15
    c: Distance(g41,g43) = 15
    c: Coincident(g41,g10)
    c: Coincident(g45,g46)
    c: Coincident(g46,g47)
    c: Coincident(g47,g48)
    c: Coincident(g48,g45)
    c: Vertical(g45)
    c: Vertical(g47)
    c: Horizontal(g46)
    c: Horizontal(g48)
    c: Distance(g45,g47) = 15
    c: Distance(g46,g48) = 15
    c: Coincident(g45,g11)
    c: Coincident(g49,g34)
    c: Coincident(g49,g46)
    c: Coincident(g50,g42)
    c: Coincident(g50,g38)
    c: Coincident(g51,g52)
    c: Coincident(g52,g53)
    c: Coincident(g53,g54)
    c: Coincident(g54,g51)
    c: Horizontal(g51)
    c: Horizontal(g53)
    c: Vertical(g52)
    c: Vertical(g54)
    c: Symmetric(g53,g51,g55)
    c: Distance(g52,g54) = 15
    c: Distance(g51,g53) = 15
    c: Symmetric(g49,g49,g55)
    c: Coincident(g56,g34)
    c: Coincident(g56,g38)
    c: Coincident(g57,g38)
    c: Coincident(g57,g46)
    c: Coincident(g58,g46)
    c: Coincident(g58,g42)
    c: Coincident(g59,g42)
    c: Coincident(g59,g34)
    c: Symmetric(g53,g53,g60)
    c: Symmetric(g35,g35,g60)
    c: Coincident(g61,g60)
    c: Symmetric(g38,g38,g61)
    c: Symmetric(g51,g51,g62)
    c: Symmetric(g42,g42,g62)
    c: Coincident(g63,g62)
    c: Symmetric(g47,g47,g63)
    c: Distance(g64) = 15
    c: Coincident(g64,g34)
    c: PointOnObject(g64,g56)
    c: Distance(g65) = 15
    c: Coincident(g65,g42)
    c: PointOnObject(g65,g58)
    c: Distance(g66) = 15
    c: Coincident(g66,g46)
    c: PointOnObject(g66,g58)
    c: Distance(g67) = 15
    c: Coincident(g67,g38)
    c: PointOnObject(g67,g56)
    c: Coincident(g68,g64)
    c: Coincident(g68,g60)
    c: Coincident(g69,g67)
    c: Coincident(g69,g60)
    c: Coincident(g70,g34)
    c: Coincident(g70,g55)
    c: Coincident(g71,g55)
    c: Coincident(g71,g42)
    c: Distance(g72) = 7.5
    c: Coincident(g72,g34)
    c: PointOnObject(g72,g59)
    c: Coincident(g73,g62)
    c: Coincident(g73,g72)
    c: Distance(g74) = 7.5
    c: Coincident(g74,g38)
    c: PointOnObject(g74,g57)
    c: Coincident(g75,g74)
    c: Coincident(g75,g62)
    c: Distance(g76) = 7.5
    c: Coincident(g76,g42)
    c: PointOnObject(g76,g59)
    c: Distance(g77) = 7.5
    c: Coincident(g77,g46)
    c: PointOnObject(g77,g57)
    c: Coincident(g78,g77)
    c: Coincident(g78,g60)
    c: Coincident(g79,g60)
    c: Coincident(g79,g76)
    c: Coincident(g80,g64)
    c: Coincident(g80,g67)
    c: Coincident(g81,g62)
    c: Coincident(g81,g65)
    c: Coincident(g82,g66)
    c: Coincident(g82,g62)
    c: Coincident(g83,g65)
    c: Coincident(g83,g66)
    c: Coincident(g84,g55)
    c: PointOnObject(g84,g73)
    c: Horizontal(g84)
    c: Coincident(g85,g55)
    c: PointOnObject(g85,g75)
    c: Horizontal(g85)
    c: Coincident(g86,g72)
    c: Coincident(g86,g84)
    c: Coincident(g87,g84)
    c: Coincident(g87,g76)
    c: Coincident(g88,g76)
    c: Coincident(g88,g72)
    c: Coincident(g89,g74)
    c: Coincident(g89,g85)
    c: Coincident(g90,g85)
    c: Coincident(g90,g77)
    c: Coincident(g91,g77)
    c: Coincident(g91,g74)
    c: Diameter(g92) = 3.5
    c: Coincident(g92,g25)
    c: Diameter(g93) = 3.5
    c: Coincident(g93,g17)
    c: Coincident(g94,g95)
    c: Coincident(g95,g96)
    c: Coincident(g96,g97)
    c: Coincident(g97,g94)
    c: Horizontal(g94)
    c: Horizontal(g96)
    c: Vertical(g95)
    c: Vertical(g97)
    c: Distance(g95,g97) = 4.5
    c: Distance(g94,g96) = 5.5
    c: Coincident(g94,g12)
    c: Diameter(g98) = 3.5
    c: Coincident(g98,g95)
    c: Distance(g99) = 152.5
    c: Coincident(g99,g95)
    c: PointOnObject(g99,g25)
    c: Distance(g100) = 85
    c: Coincident(g100,g99)
    c: Vertical(g100)
    c: Diameter(g101) = 3.5
    c: Coincident(g101,g100)
    c: Tangent(g102,g104) = 1.5708
    c: Tangent(g102,g105) = -1.5708
    c: Tangent(g103,g104) = 1.5708
    c: Tangent(g103,g105) = -1.5708
    c: Equal(g102,g103)
    c: Horizontal(g105)
    c: Distance(g102,g103) = 4
    c: Radius(g102) = 1.75
    c: Coincident(g102,g95)
FEATURE [PartDesign::Pad] Pad
  Direction = (0,0,1)
  Length = 4
  Length2 = 10
  Profile = -> Sketch
  ReferenceAxis = -> Sketch [N_Axis]
  Refine = true
  Suppressed = false
  Type = 0
FEATURE [Sketcher::SketchObject] Sketch001
  ArcFitTolerance = 1e-06
  AttachmentSupport = -> [Pad]
  FullyConstrained = true
  MakeInternals = false
  MapMode = 5
  Placement = pos=(0,0,4) rot=(0,0,1;0rad)
  sketch-geometry (96):
    g0: LineSegment [constr] StartX=0 StartY=0 StartZ=0 EndX=30 EndY=0 EndZ=0
    g1: LineSegment StartX=30 StartY=0 StartZ=0 EndX=30 EndY=30 EndZ=0
    g2: LineSegment StartX=30 StartY=30 StartZ=0 EndX=0 EndY=30 EndZ=0
    g3: LineSegment [constr] StartX=0 StartY=30 StartZ=0 EndX=0 EndY=0 EndZ=0
    g4: LineSegment StartX=0 StartY=30 StartZ=0 EndX=0 EndY=34 EndZ=0
    g5: LineSegment [constr] StartX=0 StartY=34 StartZ=0 EndX=34 EndY=34 EndZ=0
    g6: LineSegment [constr] StartX=34 StartY=34 StartZ=0 EndX=34 EndY=0 EndZ=0
    g7: LineSegment [constr] StartX=34 StartY=0 StartZ=0 EndX=30 EndY=0 EndZ=0
    g8: LineSegment [constr] StartX=34 StartY=34 StartZ=0 EndX=34 EndY=64 EndZ=0
    g9: LineSegment [constr] StartX=0 StartY=34 StartZ=0 EndX=34 EndY=64 EndZ=0
    g10: LineSegment [constr] StartX=34 StartY=64 StartZ=0 EndX=34 EndY=-33 EndZ=0
    g11: LineSegment [constr] StartX=34 StartY=-33 StartZ=0 EndX=199 EndY=-33 EndZ=0
    g12: LineSegment [constr] StartX=199 StartY=-33 StartZ=0 EndX=199 EndY=64 EndZ=0
    g13: LineSegment [constr] StartX=199 StartY=64 StartZ=0 EndX=34 EndY=64 EndZ=0
    g14: LineSegment [constr] StartX=34 StartY=64 StartZ=0 EndX=34 EndY=58.5 EndZ=0
    g15: LineSegment [constr] StartX=44.5 StartY=64 StartZ=0 EndX=34 EndY=64 EndZ=0
    g16: LineSegment [constr] StartX=199 StartY=-33 StartZ=0 EndX=199 EndY=-26.5 EndZ=0
    g17: LineSegment [constr] StartX=199 StartY=-26.5 StartZ=0 EndX=196 EndY=-26.5 EndZ=0
    g18: LineSegment [constr] StartX=196 StartY=-26.5 StartZ=0 EndX=196 EndY=-33 EndZ=0
    g19: LineSegment [constr] StartX=196 StartY=-33 StartZ=0 EndX=199 EndY=-33 EndZ=0
    g20: LineSegment [constr] StartX=199 StartY=64 StartZ=0 EndX=40 EndY=64 EndZ=0
    g21: LineSegment [constr] StartX=40 StartY=64 StartZ=0 EndX=40 EndY=-33 EndZ=0
    g22: LineSegment [constr] StartX=40 StartY=-33 StartZ=0 EndX=199 EndY=-33 EndZ=0
    g23: LineSegment [constr] StartX=199 StartY=-33 StartZ=0 EndX=199 EndY=64 EndZ=0
    g24: LineSegment [constr] StartX=40 StartY=64 StartZ=0 EndX=40 EndY=58.5 EndZ=0
    g25: LineSegment [constr] StartX=40 StartY=58.5 StartZ=0 EndX=44.5 EndY=58.5 EndZ=0
    g26: LineSegment [constr] StartX=44.5 StartY=58.5 StartZ=0 EndX=44.5 EndY=64 EndZ=0
    g27: LineSegment [constr] StartX=44.5 StartY=64 StartZ=0 EndX=40 EndY=64 EndZ=0
    g28: LineSegment [constr] StartX=34 StartY=-33 StartZ=0 EndX=30 EndY=-33 EndZ=0
    g29: LineSegment StartX=30 StartY=0 StartZ=0 EndX=30 EndY=-33 EndZ=0
    g30: LineSegment StartX=30 StartY=-33 StartZ=0 EndX=30 EndY=-37 EndZ=0
    g31: LineSegment StartX=30 StartY=-37 StartZ=0 EndX=199 EndY=-37 EndZ=0
    g32: LineSegment [constr] StartX=199 StartY=-37 StartZ=0 EndX=199 EndY=-33 EndZ=0
    g33: LineSegment [constr] StartX=34 StartY=64 StartZ=0 EndX=34 EndY=49 EndZ=0
    g34: LineSegment [constr] StartX=34 StartY=49 StartZ=0 EndX=49 EndY=49 EndZ=0
    g35: LineSegment [constr] StartX=49 StartY=49 StartZ=0 EndX=49 EndY=64 EndZ=0
    g36: LineSegment [constr] StartX=49 StartY=64 StartZ=0 EndX=34 EndY=64 EndZ=0
    g37: LineSegment [constr] StartX=199 StartY=64 StartZ=0 EndX=184 EndY=64 EndZ=0
    g38: LineSegment [constr] StartX=184 StartY=64 StartZ=0 EndX=184 EndY=49 EndZ=0
    g39: LineSegment [constr] StartX=184 StartY=49 StartZ=0 EndX=199 EndY=49 EndZ=0
    g40: LineSegment [constr] StartX=199 StartY=49 StartZ=0 EndX=199 EndY=64 EndZ=0
    g41: LineSegment [constr] StartX=34 StartY=-33 StartZ=0 EndX=49 EndY=-33 EndZ=0
    g42: LineSegment [constr] StartX=49 StartY=-33 StartZ=0 EndX=49 EndY=-18 EndZ=0
    g43: LineSegment [constr] StartX=49 StartY=-18 StartZ=0 EndX=34 EndY=-18 EndZ=0
    g44: LineSegment [constr] StartX=34 StartY=-18 StartZ=0 EndX=34 EndY=-33 EndZ=0
    g45: LineSegment [constr] StartX=199 StartY=-33 StartZ=0 EndX=199 EndY=-18 EndZ=0
    g46: LineSegment [constr] StartX=199 StartY=-18 StartZ=0 EndX=184 EndY=-18 EndZ=0
    g47: LineSegment [constr] StartX=184 StartY=-18 StartZ=0 EndX=184 EndY=-33 EndZ=0
    g48: LineSegment [constr] StartX=184 StartY=-33 StartZ=0 EndX=199 EndY=-33 EndZ=0
    g49: LineSegment [constr] StartX=49 StartY=49 StartZ=0 EndX=184 EndY=-18 EndZ=0
    g50: LineSegment [constr] StartX=49 StartY=-18 StartZ=0 EndX=184 EndY=49 EndZ=0
    g51: LineSegment [constr] StartX=109 StartY=8 StartZ=0 EndX=124 EndY=8 EndZ=0
    g52: LineSegment [constr] StartX=124 StartY=8 StartZ=0 EndX=124 EndY=23 EndZ=0
    g53: LineSegment [constr] StartX=124 StartY=23 StartZ=0 EndX=109 EndY=23 EndZ=0
    g54: LineSegment [constr] StartX=109 StartY=23 StartZ=0 EndX=109 EndY=8 EndZ=0
    g55: GeomPoint [constr] X=116.5 Y=15.5 Z=0
    g56: LineSegment [constr] StartX=49 StartY=49 StartZ=0 EndX=184 EndY=49 EndZ=0
    g57: LineSegment [constr] StartX=184 StartY=49 StartZ=0 EndX=184 EndY=-18 EndZ=0
    g58: LineSegment [constr] StartX=184 StartY=-18 StartZ=0 EndX=49 EndY=-18 EndZ=0
    g59: LineSegment [constr] StartX=49 StartY=-18 StartZ=0 EndX=49 EndY=49 EndZ=0
    g60: LineSegment [constr] StartX=116.5 StartY=23 StartZ=0 EndX=49 EndY=56.5 EndZ=0
    g61: LineSegment [constr] StartX=116.5 StartY=23 StartZ=0 EndX=184 EndY=56.5 EndZ=0
    g62: LineSegment [constr] StartX=116.5 StartY=8 StartZ=0 EndX=49 EndY=-25.5 EndZ=0
    g63: LineSegment [constr] StartX=116.5 StartY=8 StartZ=0 EndX=184 EndY=-25.5 EndZ=0
    g64: LineSegment [constr] StartX=49 StartY=49 StartZ=0 EndX=64 EndY=49 EndZ=0
    g65: LineSegment [constr] StartX=49 StartY=-18 StartZ=0 EndX=64 EndY=-18 EndZ=0
    g66: LineSegment [constr] StartX=184 StartY=-18 StartZ=0 EndX=169 EndY=-18 EndZ=0
    g67: LineSegment [constr] StartX=184 StartY=49 StartZ=0 EndX=169 EndY=49 EndZ=0
    g68: LineSegment [constr] StartX=64 StartY=49 StartZ=0 EndX=116.5 EndY=23 EndZ=0
    g69: LineSegment [constr] StartX=169 StartY=49 StartZ=0 EndX=116.5 EndY=23 EndZ=0
    g70: LineSegment [constr] StartX=49 StartY=49 StartZ=0 EndX=116.5 EndY=15.5 EndZ=0
    g71: LineSegment [constr] StartX=116.5 StartY=15.5 StartZ=0 EndX=49 EndY=-18 EndZ=0
    g72: LineSegment [constr] StartX=49 StartY=49 StartZ=0 EndX=49 EndY=41.5 EndZ=0
    g73: LineSegment [constr] StartX=116.5 StartY=8 StartZ=0 EndX=49 EndY=41.5 EndZ=0
    g74: LineSegment [constr] StartX=184 StartY=49 StartZ=0 EndX=184 EndY=41.5 EndZ=0
    g75: LineSegment [constr] StartX=184 StartY=41.5 StartZ=0 EndX=116.5 EndY=8 EndZ=0
    g76: LineSegment [constr] StartX=49 StartY=-18 StartZ=0 EndX=49 EndY=-10.5 EndZ=0
    g77: LineSegment [constr] StartX=184 StartY=-18 StartZ=0 EndX=184 EndY=-10.5 EndZ=0
    g78: LineSegment [constr] StartX=184 StartY=-10.5 StartZ=0 EndX=116.5 EndY=23 EndZ=0
    g79: LineSegment [constr] StartX=116.5 StartY=23 StartZ=0 EndX=49 EndY=-10.5 EndZ=0
    g80: LineSegment [constr] StartX=64 StartY=49 StartZ=0 EndX=169 EndY=49 EndZ=0
    g81: LineSegment [constr] StartX=116.5 StartY=8 StartZ=0 EndX=64 EndY=-18 EndZ=0
    g82: LineSegment [constr] StartX=169 StartY=-18 StartZ=0 EndX=116.5 EndY=8 EndZ=0
    g83: LineSegment [constr] StartX=64 StartY=-18 StartZ=0 EndX=169 EndY=-18 EndZ=0
    g84: LineSegment [constr] StartX=116.5 StartY=15.5 StartZ=0 EndX=101.388 EndY=15.5 EndZ=0
    g85: LineSegment [constr] StartX=116.5 StartY=15.5 StartZ=0 EndX=131.612 EndY=15.5 EndZ=0
    g86: LineSegment [constr] StartX=49 StartY=41.5 StartZ=0 EndX=101.388 EndY=15.5 EndZ=0
    g87: LineSegment [constr] StartX=101.388 StartY=15.5 StartZ=0 EndX=49 EndY=-10.5 EndZ=0
    g88: LineSegment [constr] StartX=49 StartY=-10.5 StartZ=0 EndX=49 EndY=41.5 EndZ=0
    g89: LineSegment [constr] StartX=184 StartY=41.5 StartZ=0 EndX=131.612 EndY=15.5 EndZ=0
    g90: LineSegment [constr] StartX=131.612 StartY=15.5 StartZ=0 EndX=184 EndY=-10.5 EndZ=0
    g91: LineSegment [constr] StartX=184 StartY=-10.5 StartZ=0 EndX=184 EndY=41.5 EndZ=0
    g92: LineSegment StartX=0 StartY=34 StartZ=0 EndX=34 EndY=34 EndZ=0
    g93: LineSegment StartX=34 StartY=34 StartZ=0 EndX=34 EndY=-33 EndZ=0
    g94: LineSegment StartX=199 StartY=-33 StartZ=0 EndX=34 EndY=-33 EndZ=0
    g95: LineSegment StartX=199 StartY=-33 StartZ=0 EndX=199 EndY=-37 EndZ=0
  constraints (240):
    c: Coincident(g0,g1)
    c: Coincident(g1,g2)
    c: Coincident(g2,g3)
    c: Coincident(g3,g0)
    c: Horizontal(g0)
    c: Horizontal(g2)
    c: Vertical(g1)
    c: Vertical(g3)
    c: Distance(g1,g3) = 30
    c: Distance(g0,g2) = 30
    c: Coincident(g0,g-1)
    c: Distance(g4) = 4
    c: Coincident(g4,g2)
    c: PointOnObject(g4,g-2)
    c: Distance(g5) = 34
    c: Coincident(g5,g4)
    c: Horizontal(g5)
    c: Coincident(g6,g5)
    c: PointOnObject(g6,g-1)
    c: Vertical(g6)
    c: Coincident(g7,g6)
    c: Coincident(g7,g0)
    c: Distance(g8) = 30
    c: Coincident(g8,g5)
    c: Vertical(g8)
    c: Coincident(g9,g4)
    c: Coincident(g9,g8)
    c: Coincident(g10,g11)
    c: Coincident(g11,g12)
    c: Coincident(g12,g13)
    c: Coincident(g13,g10)
    c: Vertical(g10)
    c: Vertical(g12)
    c: Horizontal(g11)
    c: Horizontal(g13)
    c: Distance(g10,g12) = 165
    c: Distance(g11,g13) = 97
    c: Coincident(g10,g8)
    c: Coincident(g15,g14)
    c: Vertical(g14)
    c: Horizontal(g15)
    c: Distance(g14,g15) = 10.5
    c: Distance(g14,g15) = 5.5
    c: Coincident(g14,g8)
    c: Coincident(g16,g17)
    c: Coincident(g17,g18)
    c: Coincident(g18,g19)
    c: Coincident(g19,g16)
    c: Vertical(g16)
    c: Vertical(g18)
    c: Horizontal(g17)
    c: Horizontal(g19)
    c: Distance(g16,g18) = 3
    c: Distance(g17,g19) = 6.5
    c: Coincident(g16,g11)
    c: Coincident(g20,g21)
    c: Coincident(g21,g22)
    c: Coincident(g22,g23)
    c: Coincident(g23,g20)
    c: Horizontal(g20)
    c: Horizontal(g22)
    c: Vertical(g21)
    c: Vertical(g23)
    c: Distance(g21,g23) = 159
    c: Coincident(g20,g12)
    c: PointOnObject(g21,g11)
    c: Coincident(g24,g25)
    c: Coincident(g25,g26)
    c: Coincident(g26,g27)
    c: Coincident(g27,g24)
    c: Vertical(g24)
    c: Vertical(g26)
    c: Horizontal(g25)
    c: Horizontal(g27)
    c: Distance(g24,g26) = 4.5
    c: Distance(g25,g27) = 5.5
    c: Coincident(g24,g20)
    c: Distance(g28) = 4
    c: Coincident(g28,g10)
    c: Horizontal(g28)
    c: Coincident(g29,g0)
    c: Coincident(g29,g28)
    c: Distance(g30) = 4
    c: Coincident(g30,g28)
    c: Vertical(g30)
    c: Distance(g31) = 169
    c: Coincident(g31,g30)
    c: Horizontal(g31)
    c: Coincident(g32,g31)
    c: Coincident(g32,g11)
    c: Coincident(g33,g34)
    c: Coincident(g34,g35)
    c: Coincident(g35,g36)
    c: Coincident(g36,g33)
    c: Vertical(g33)
    c: Vertical(g35)
    c: Horizontal(g34)
    c: Horizontal(g36)
    c: Distance(g33,g35) = 15
    c: Distance(g34,g36) = 15
    c: Coincident(g33,g8)
    c: Coincident(g37,g38)
    c: Coincident(g38,g39)
    c: Coincident(g39,g40)
    c: Coincident(g40,g37)
    c: Horizontal(g37)
    c: Horizontal(g39)
    c: Vertical(g38)
    c: Vertical(g40)
    c: Distance(g38,g40) = 15
    c: Distance(g37,g39) = 15
    c: Coincident(g37,g12)
    c: Coincident(g41,g42)
    c: Coincident(g42,g43)
    c: Coincident(g43,g44)
    c: Coincident(g44,g41)
    c: Horizontal(g41)
    c: Horizontal(g43)
    c: Vertical(g42)
    c: Vertical(g44)
    c: Distance(g42,g44) = 15
    c: Distance(g41,g43) = 15
    c: Coincident(g41,g10)
    c: Coincident(g45,g46)
    c: Coincident(g46,g47)
    c: Coincident(g47,g48)
    c: Coincident(g48,g45)
    c: Vertical(g45)
    c: Vertical(g47)
    c: Horizontal(g46)
    c: Horizontal(g48)
    c: Distance(g45,g47) = 15
    c: Distance(g46,g48) = 15
    c: Coincident(g45,g11)
    c: Coincident(g49,g34)
    c: Coincident(g49,g46)
    c: Coincident(g50,g42)
    c: Coincident(g50,g38)
    c: Coincident(g51,g52)
    c: Coincident(g52,g53)
    c: Coincident(g53,g54)
    c: Coincident(g54,g51)
    c: Horizontal(g51)
    c: Horizontal(g53)
    c: Vertical(g52)
    c: Vertical(g54)
    c: Symmetric(g53,g51,g55)
    c: Distance(g52,g54) = 15
    c: Distance(g51,g53) = 15
    c: Symmetric(g49,g49,g55)
    c: Coincident(g56,g34)
    c: Coincident(g56,g38)
    c: Coincident(g57,g38)
    c: Coincident(g57,g46)
    c: Coincident(g58,g46)
    c: Coincident(g58,g42)
    c: Coincident(g59,g42)
    c: Coincident(g59,g34)
    c: Symmetric(g53,g53,g60)
    c: Symmetric(g35,g35,g60)
    c: Coincident(g61,g60)
    c: Symmetric(g38,g38,g61)
    c: Symmetric(g51,g51,g62)
    c: Symmetric(g42,g42,g62)
    c: Coincident(g63,g62)
    c: Symmetric(g47,g47,g63)
    c: Distance(g64) = 15
    c: Coincident(g64,g34)
    c: PointOnObject(g64,g56)
    c: Distance(g65) = 15
    c: Coincident(g65,g42)
    c: PointOnObject(g65,g58)
    c: Distance(g66) = 15
    c: Coincident(g66,g46)
    c: PointOnObject(g66,g58)
    c: Distance(g67) = 15
    c: Coincident(g67,g38)
    c: PointOnObject(g67,g56)
    c: Coincident(g68,g64)
    c: Coincident(g68,g60)
    c: Coincident(g69,g67)
    c: Coincident(g69,g60)
    c: Coincident(g70,g34)
    c: Coincident(g70,g55)
    c: Coincident(g71,g55)
    c: Coincident(g71,g42)
    c: Distance(g72) = 7.5
    c: Coincident(g72,g34)
    c: PointOnObject(g72,g59)
    c: Coincident(g73,g62)
    c: Coincident(g73,g72)
    c: Distance(g74) = 7.5
    c: Coincident(g74,g38)
    c: PointOnObject(g74,g57)
    c: Coincident(g75,g74)
    c: Coincident(g75,g62)
    c: Distance(g76) = 7.5
    c: Coincident(g76,g42)
    c: PointOnObject(g76,g59)
    c: Distance(g77) = 7.5
    c: Coincident(g77,g46)
    c: PointOnObject(g77,g57)
    c: Coincident(g78,g77)
    c: Coincident(g78,g60)
    c: Coincident(g79,g60)
    c: Coincident(g79,g76)
    c: Coincident(g80,g64)
    c: Coincident(g80,g67)
    c: Coincident(g81,g62)
    c: Coincident(g81,g65)
    c: Coincident(g82,g66)
    c: Coincident(g82,g62)
    c: Coincident(g83,g65)
    c: Coincident(g83,g66)
    c: Coincident(g84,g55)
    c: PointOnObject(g84,g73)
    c: Horizontal(g84)
    c: Coincident(g85,g55)
    c: PointOnObject(g85,g75)
    c: Horizontal(g85)
    c: Coincident(g86,g72)
    c: Coincident(g86,g84)
    c: Coincident(g87,g84)
    c: Coincident(g87,g76)
    c: Coincident(g88,g76)
    c: Coincident(g88,g72)
    c: Coincident(g89,g74)
    c: Coincident(g89,g85)
    c: Coincident(g90,g85)
    c: Coincident(g90,g77)
    c: Coincident(g91,g77)
    c: Coincident(g91,g74)
    c: Coincident(g92,g4)
    c: Coincident(g92,g5)
    c: Coincident(g93,g5)
    c: Coincident(g93,g10)
    c: Coincident(g94,g11)
    c: Coincident(g94,g10)
    c: Coincident(g95,g11)
    c: Coincident(g95,g31)
FEATURE [PartDesign::Pad] Pad001
  BaseFeature = -> Pad
  Direction = (0,0,1)
  Length = 34
  Length2 = 10
  Profile = -> Sketch001
  ReferenceAxis = -> Sketch001 [N_Axis]
  Refine = true
  Reversed = true
  Suppressed = false
  Type = 0
FEATURE [PartDesign::Fillet] Fillet
  Base = -> Pad001 [Edge43,Edge44,Edge46,Edge50,Edge49,Edge52,Edge58,Edge61,Edge62,Edge56,Edge55,Edge64]
  BaseFeature = -> Pad001
  Radius = 3
  Refine = true
  SupportTransform = false
  Suppressed = false
  UseAllEdges = false
FEATURE [Sketcher::SketchObject] Sketch004
  ArcFitTolerance = 1e-06
  FullyConstrained = true
  MakeInternals = false
  MapMode = 5
  Placement = pos=(0,64,0) rot=(0,0.707107,0.707107;3.14159rad)
  sketch-geometry (10):
    g0: LineSegment [constr] StartX=0 StartY=0 StartZ=0 EndX=0 EndY=4 EndZ=0
    g1: LineSegment [constr] StartX=0 StartY=4 StartZ=0 EndX=-30 EndY=4 EndZ=0
    g2: LineSegment [constr] StartX=-30 StartY=4 StartZ=0 EndX=-30 EndY=0 EndZ=0
    g3: LineSegment [constr] StartX=-30 StartY=0 StartZ=0 EndX=0 EndY=0 EndZ=0
    g4: LineSegment [constr] StartX=0 StartY=4 StartZ=0 EndX=0 EndY=34 EndZ=0
    g5: LineSegment [constr] StartX=0 StartY=34 StartZ=0 EndX=-30 EndY=34 EndZ=0
    g6: LineSegment [constr] StartX=-30 StartY=34 StartZ=0 EndX=-30 EndY=4 EndZ=0
    g7: LineSegment [constr] StartX=-30 StartY=4 StartZ=0 EndX=0 EndY=4 EndZ=0
    g8: LineSegment [constr] StartX=-30 StartY=34 StartZ=0 EndX=-1.6e-15 EndY=4 EndZ=0
    g9: Circle CenterX=-15 CenterY=19 CenterZ=0 NormalX=0 NormalY=0 NormalZ=1 AngleXU=0 Radius=2.5
  constraints (26):
    c: Coincident(g0,g1)
    c: Coincident(g1,g2)
    c: Coincident(g2,g3)
    c: Coincident(g3,g0)
    c: Vertical(g0)
    c: Vertical(g2)
    c: Horizontal(g1)
    c: Horizontal(g3)
    c: Distance(g0,g2) = 30
    c: Distance(g1,g3) = 4
    c: Coincident(g0,g-1)
    c: Coincident(g4,g5)
    c: Coincident(g5,g6)
    c: Coincident(g6,g7)
    c: Coincident(g7,g4)
    c: Vertical(g4)
    c: Vertical(g6)
    c: Horizontal(g5)
    c: Horizontal(g7)
    c: Distance(g4,g6) = 30
    c: Distance(g5,g7) = 30
    c: Coincident(g4,g0)
    c: Coincident(g8,g5)
    c: Coincident(g8,g0)
    c: Diameter(g9) = 5
    c: Symmetric(g8,g8,g9)
FEATURE [Sketcher::SketchObject] Sketch005
  ArcFitTolerance = 1e-06
  AttachmentSupport = -> [Pad001]
  FullyConstrained = true
  MakeInternals = false
  MapMode = 5
  Placement = pos=(0,0,0) rot=(1,0,0;3.14159rad)
FEATURE [PartDesign::Chamfer] Chamfer
  Angle = 45
  Base = -> Fillet [Edge51]
  BaseFeature = -> Fillet
  ChamferType = 0
  FlipDirection = false
  Refine = true
  Size = 3
  Size2 = 1
  SupportTransform = false
  Suppressed = false
  UseAllEdges = false
FEATURE [Sketcher::SketchObject] Sketch006
  ArcFitTolerance = 1e-06
  AttachmentSupport = -> [Chamfer]
  FullyConstrained = true
  MakeInternals = false
  MapMode = 5
  Placement = pos=(0,34,0) rot=(0,0.707107,0.707107;3.14159rad)
  sketch-geometry (10):
    g0: LineSegment [constr] StartX=0 StartY=0 StartZ=0 EndX=-34 EndY=0 EndZ=0
    g1: LineSegment [constr] StartX=-34 StartY=0 StartZ=0 EndX=-34 EndY=-30 EndZ=0
    g2: LineSegment [constr] StartX=-34 StartY=-30 StartZ=0 EndX=0 EndY=-30 EndZ=0
    g3: LineSegment [constr] StartX=0 StartY=-30 StartZ=0 EndX=0 EndY=0 EndZ=0
    g4: LineSegment [constr] StartX=-34 StartY=0 StartZ=0 EndX=-34 EndY=-30 EndZ=0
    g5: LineSegment [constr] StartX=-34 StartY=-30 StartZ=0 EndX=-30 EndY=-30 EndZ=0
    g6: LineSegment [constr] StartX=-30 StartY=-30 StartZ=0 EndX=-30 EndY=0 EndZ=0
    g7: LineSegment [constr] StartX=-30 StartY=0 StartZ=0 EndX=-34 EndY=0 EndZ=0
    g8: LineSegment [constr] StartX=-30 StartY=0 StartZ=0 EndX=-1.6e-15 EndY=-30 EndZ=0
    g9: Circle CenterX=-15 CenterY=-15 CenterZ=0 NormalX=0 NormalY=0 NormalZ=1 AngleXU=0 Radius=2.75
  constraints (26):
    c: Coincident(g0,g1)
    c: Coincident(g1,g2)
    c: Coincident(g2,g3)
    c: Coincident(g3,g0)
    c: Horizontal(g0)
    c: Horizontal(g2)
    c: Vertical(g1)
    c: Vertical(g3)
    c: Distance(g1,g3) = 34
    c: Distance(g0,g2) = 30
    c: Coincident(g0,g-1)
    c: Coincident(g4,g5)
    c: Coincident(g5,g6)
    c: Coincident(g6,g7)
    c: Coincident(g7,g4)
    c: Vertical(g4)
    c: Vertical(g6)
    c: Horizontal(g5)
    c: Horizontal(g7)
    c: Distance(g4,g6) = 4
    c: Coincident(g4,g0)
    c: PointOnObject(g5,g2)
    c: Coincident(g8,g6)
    c: Coincident(g8,g2)
    c: Diameter(g9) = 5.5
    c: Symmetric(g8,g8,g9)
FEATURE [PartDesign::Hole] Hole
  BaseFeature = -> Chamfer
  CustomThreadClearance = 0
  Depth = 25
  DepthType = 0
  Diameter = 5.8
  DrillForDepth = false
  DrillPoint = 1
  DrillPointAngle = 118
  HoleCutCountersinkAngle = 90
  HoleCutCustomValues = false
  HoleCutDepth = 0
  HoleCutDiameter = 6.1
  HoleCutType = 0
  ModelThread = false
  Profile = -> Sketch006
  Refine = true
  Suppressed = false
  Tapered = false
  TaperedAngle = 90
  ThreadClass = 0
  ThreadDepth = 25
  ThreadDepthType = 0
  ThreadDirection = 0
  ThreadFit = 2
  ThreadSize = 13
  ThreadType = 1
  Threaded = false
  UseCustomThreadClearance = false
FEATURE [Sketcher::SketchObject] Sketch007
  ArcFitTolerance = 1e-06
  AttachmentSupport = -> [Hole]
  FullyConstrained = true
  MakeInternals = false
  MapMode = 5
  Placement = pos=(0,-33,0) rot=(0,0.707107,0.707107;3.14159rad)
  sketch-geometry (16):
    g0: LineSegment [constr] StartX=0 StartY=0 StartZ=0 EndX=-34 EndY=0 EndZ=0
    g1: LineSegment [constr] StartX=-34 StartY=0 StartZ=0 EndX=-34 EndY=-26 EndZ=0
    g2: LineSegment [constr] StartX=-34 StartY=-26 StartZ=0 EndX=0 EndY=-26 EndZ=0
    g3: LineSegment [constr] StartX=0 StartY=-26 StartZ=0 EndX=0 EndY=0 EndZ=0
    g4: LineSegment [constr] StartX=-34 StartY=0 StartZ=0 EndX=-199 EndY=0 EndZ=0
    g5: LineSegment [constr] StartX=-199 StartY=0 StartZ=0 EndX=-199 EndY=-30 EndZ=0
    g6: LineSegment [constr] StartX=-199 StartY=-30 StartZ=0 EndX=-34 EndY=-30 EndZ=0
    g7: LineSegment [constr] StartX=-34 StartY=-30 StartZ=0 EndX=-34 EndY=0 EndZ=0
    g8: LineSegment [constr] StartX=-199 StartY=0 StartZ=0 EndX=-177 EndY=0 EndZ=0
    g9: LineSegment [constr] StartX=-177 StartY=0 StartZ=0 EndX=-60 EndY=0 EndZ=0
    g10: LineSegment [constr] StartX=-177 StartY=0 StartZ=0 EndX=-177 EndY=-15 EndZ=0
    g11: LineSegment [constr] StartX=-60 StartY=0 StartZ=0 EndX=-60 EndY=-6 EndZ=0
    g12: LineSegment [constr] StartX=-60 StartY=-6 StartZ=0 EndX=-60 EndY=-24 EndZ=0
    g13: Circle CenterX=-177 CenterY=-15 CenterZ=0 NormalX=0 NormalY=0 NormalZ=1 AngleXU=0 Radius=1.5
    g14: Circle CenterX=-60 CenterY=-6 CenterZ=0 NormalX=0 NormalY=0 NormalZ=1 AngleXU=0 Radius=1.5
    g15: Circle CenterX=-60 CenterY=-24 CenterZ=0 NormalX=0 NormalY=0 NormalZ=1 AngleXU=0 Radius=1.5
  constraints (43):
    c: Coincident(g0,g1)
    c: Coincident(g1,g2)
    c: Coincident(g2,g3)
    c: Coincident(g3,g0)
    c: Horizontal(g0)
    c: Horizontal(g2)
    c: Vertical(g1)
    c: Vertical(g3)
    c: Distance(g1,g3) = 34
    c: Distance(g0,g2) = 26
    c: Coincident(g0,g-1)
    c: Coincident(g4,g5)
    c: Coincident(g5,g6)
    c: Coincident(g6,g7)
    c: Coincident(g7,g4)
    c: Horizontal(g4)
    c: Horizontal(g6)
    c: Vertical(g5)
    c: Vertical(g7)
    c: Distance(g5,g7) = 165
    c: Distance(g4,g6) = 30
    c: Coincident(g4,g0)
    c: Distance(g8) = 22
    c: Coincident(g8,g4)
    c: PointOnObject(g8,g4)
    c: Distance(g9) = 117
    c: Coincident(g9,g8)
    c: PointOnObject(g9,g4)
    c: Distance(g10) = 15
    c: Coincident(g10,g8)
    c: Vertical(g10)
    c: Distance(g11) = 6
    c: Coincident(g11,g9)
    c: Vertical(g11)
    c: Distance(g12) = 18
    c: Coincident(g12,g11)
    c: Vertical(g12)
    c: Diameter(g13) = 3
    c: Coincident(g13,g10)
    c: Diameter(g14) = 3
    c: Coincident(g14,g11)
    c: Diameter(g15) = 3
    c: Coincident(g15,g12)
FEATURE [PartDesign::Hole] Hole001
  BaseFeature = -> Hole
  CustomThreadClearance = 0
  Depth = 25
  DepthType = 0
  Diameter = 3.6
  DrillForDepth = false
  DrillPoint = 1
  DrillPointAngle = 118
  HoleCutCountersinkAngle = 90
  HoleCutCustomValues = false
  HoleCutDepth = 0
  HoleCutDiameter = 6.1
  HoleCutType = 0
  ModelThread = false
  Profile = -> Sketch007
  Refine = true
  Suppressed = false
  Tapered = false
  TaperedAngle = 90
  ThreadClass = 0
  ThreadDepth = 25
  ThreadDepthType = 0
  ThreadDirection = 0
  ThreadFit = 2
  ThreadSize = 9
  ThreadType = 1
  Threaded = false
  UseCustomThreadClearance = false
FEATURE [PartDesign::Chamfer] Chamfer001
  Angle = 45
  Base = -> Hole001 [Edge125,Edge49]
  BaseFeature = -> Hole001
  ChamferType = 0
  FlipDirection = false
  Refine = true
  Size = 3
  Size2 = 1
  SupportTransform = false
  Suppressed = false
  UseAllEdges = false
FEATURE [PartDesign::Chamfer] Chamfer002
  Angle = 45
  Base = -> Chamfer001 [Edge45]
  BaseFeature = -> Chamfer001
  ChamferType = 0
  FlipDirection = false
  Refine = true
  Size = 7
  Size2 = 1
  SupportTransform = false
  Suppressed = false
  UseAllEdges = false
FEATURE [Sketcher::SketchObject] Sketch008
  ArcFitTolerance = 1e-06
  AttachmentSupport = -> [Chamfer002]
  FullyConstrained = true
  MakeInternals = false
  MapMode = 5
  Placement = pos=(0,0,4) rot=(0,0,1;0rad)
  sketch-geometry (10):
    g0: LineSegment [constr] StartX=0 StartY=0 StartZ=0 EndX=0 EndY=-37 EndZ=0
    g1: LineSegment [constr] StartX=0 StartY=-37 StartZ=0 EndX=30 EndY=-37 EndZ=0
    g2: LineSegment [constr] StartX=30 StartY=-37 StartZ=0 EndX=30 EndY=0 EndZ=0
    g3: LineSegment [constr] StartX=30 StartY=0 StartZ=0 EndX=0 EndY=0 EndZ=0
    g4: LineSegment [constr] StartX=30 StartY=-37 StartZ=0 EndX=114.5 EndY=-37 EndZ=0
    g5: LineSegment [constr] StartX=114.5 StartY=-37 StartZ=0 EndX=119.5 EndY=-37 EndZ=0
    g6: LineSegment StartX=119.5 StartY=-37 StartZ=0 EndX=109.5 EndY=-37 EndZ=0
    g7: LineSegment StartX=109.5 StartY=-37 StartZ=0 EndX=109.5 EndY=-47 EndZ=0
    g8: LineSegment StartX=109.5 StartY=-47 StartZ=0 EndX=119.5 EndY=-47 EndZ=0
    g9: LineSegment StartX=119.5 StartY=-47 StartZ=0 EndX=119.5 EndY=-37 EndZ=0
  constraints (28):
    c: Coincident(g0,g1)
    c: Coincident(g1,g2)
    c: Coincident(g2,g3)
    c: Coincident(g3,g0)
    c: Vertical(g0)
    c: Vertical(g2)
    c: Horizontal(g1)
    c: Horizontal(g3)
    c: Distance(g0,g2) = 30
    c: Distance(g1,g3) = 37
    c: Coincident(g0,g-1)
    c: Distance(g4) = 84.5
    c: Coincident(g4,g1)
    c: Horizontal(g4)
    c: Distance(g5) = 5
    c: Coincident(g5,g4)
    c: Horizontal(g5)
    c: Coincident(g6,g7)
    c: Coincident(g7,g8)
    c: Coincident(g8,g9)
    c: Coincident(g9,g6)
    c: Horizontal(g6)
    c: Horizontal(g8)
    c: Vertical(g7)
    c: Vertical(g9)
    c: Distance(g7,g9) = 10
    c: Distance(g6,g8) = 10
    c: Coincident(g6,g5)
FEATURE [PartDesign::Pad] Pad002
  BaseFeature = -> Chamfer002
  Direction = (0,0,1)
  Length = 4
  Length2 = 10
  Profile = -> Sketch008
  ReferenceAxis = -> Sketch008 [N_Axis]
  Refine = true
  Reversed = true
  Suppressed = false
  Type = 0
FEATURE [Sketcher::SketchObject] Sketch009
  ArcFitTolerance = 1e-06
  AttachmentSupport = -> [Pad002]
  FullyConstrained = true
  MakeInternals = false
  MapMode = 5
  Placement = pos=(0,0,0) rot=(1,0,0;3.14159rad)
  sketch-geometry (9):
    g0: LineSegment [constr] StartX=0 StartY=0 StartZ=0 EndX=109.5 EndY=0 EndZ=0
    g1: LineSegment [constr] StartX=109.5 StartY=0 StartZ=0 EndX=109.5 EndY=37 EndZ=0
    g2: LineSegment [constr] StartX=109.5 StartY=37 StartZ=0 EndX=0 EndY=37 EndZ=0
    g3: LineSegment [constr] StartX=0 StartY=37 StartZ=0 EndX=0 EndY=0 EndZ=0
    g4: LineSegment [constr] StartX=109.5 StartY=37 StartZ=0 EndX=109.5 EndY=43 EndZ=0
    g5: LineSegment StartX=109.5 StartY=43 StartZ=0 EndX=119.5 EndY=43 EndZ=0
    g6: LineSegment StartX=119.5 StartY=43 StartZ=0 EndX=119.5 EndY=47 EndZ=0
    g7: LineSegment StartX=119.5 StartY=47 StartZ=0 EndX=109.5 EndY=47 EndZ=0
    g8: LineSegment StartX=109.5 StartY=47 StartZ=0 EndX=109.5 EndY=43 EndZ=0
  constraints (25):
    c: Coincident(g0,g1)
    c: Coincident(g1,g2)
    c: Coincident(g2,g3)
    c: Coincident(g3,g0)
    c: Horizontal(g0)
    c: Horizontal(g2)
    c: Vertical(g1)
    c: Vertical(g3)
    c: Distance(g1,g3) = 109.5
    c: Distance(g0,g2) = 37
    c: Coincident(g0,g-1)
    c: Distance(g4) = 6
    c: Coincident(g4,g1)
    c: Vertical(g4)
    c: Coincident(g5,g6)
    c: Coincident(g6,g7)
    c: Coincident(g7,g8)
    c: Coincident(g8,g5)
    c: Horizontal(g5)
    c: Horizontal(g7)
    c: Vertical(g6)
    c: Vertical(g8)
    c: Distance(g6,g8) = 10
    c: Distance(g5,g7) = 4
    c: Coincident(g5,g4)
FEATURE [PartDesign::Pad] Pad003
  BaseFeature = -> Pad002
  Direction = (0,0,-1)
  Length = 30
  Length2 = 10
  Profile = -> Sketch009
  ReferenceAxis = -> Sketch009 [N_Axis]
  Refine = true
  Suppressed = false
  Type = 0
FEATURE [Sketcher::SketchObject] Sketch010
  ArcFitTolerance = 1e-06
  AttachmentSupport = -> [Pad003]
  FullyConstrained = true
  MakeInternals = false
  MapMode = 5
  Placement = pos=(0,-43,0) rot=(0,0.707107,0.707107;3.14159rad)
  sketch-geometry (8):
    g0: LineSegment [constr] StartX=0 StartY=0 StartZ=0 EndX=-109.5 EndY=0 EndZ=0
    g1: LineSegment [constr] StartX=-109.5 StartY=0 StartZ=0 EndX=-109.5 EndY=-30 EndZ=0
    g2: LineSegment [constr] StartX=-109.5 StartY=-30 StartZ=0 EndX=0 EndY=-30 EndZ=0
    g3: LineSegment [constr] StartX=0 StartY=-30 StartZ=0 EndX=0 EndY=0 EndZ=0
    g4: LineSegment StartX=-109.5 StartY=-30 StartZ=0 EndX=-109.5 EndY=-26 EndZ=0
    g5: LineSegment StartX=-109.5 StartY=-26 StartZ=0 EndX=-119.5 EndY=-26 EndZ=0
    g6: LineSegment StartX=-119.5 StartY=-26 StartZ=0 EndX=-119.5 EndY=-30 EndZ=0
    g7: LineSegment StartX=-119.5 StartY=-30 StartZ=0 EndX=-109.5 EndY=-30 EndZ=0
  constraints (22):
    c: Coincident(g0,g1)
    c: Coincident(g1,g2)
    c: Coincident(g2,g3)
    c: Coincident(g3,g0)
    c: Horizontal(g0)
    c: Horizontal(g2)
    c: Vertical(g1)
    c: Vertical(g3)
    c: Distance(g1,g3) = 109.5
    c: Distance(g0,g2) = 30
    c: Coincident(g0,g-1)
    c: Coincident(g4,g5)
    c: Coincident(g5,g6)
    c: Coincident(g6,g7)
    c: Coincident(g7,g4)
    c: Vertical(g4)
    c: Vertical(g6)
    c: Horizontal(g5)
    c: Horizontal(g7)
    c: Distance(g4,g6) = 10
    c: Distance(g5,g7) = 4
    c: Coincident(g4,g1)
FEATURE [PartDesign::Pad] Pad004
  BaseFeature = -> Pad003
  Direction = (0,1,-2e-16)
  Length = 4
  Length2 = 10
  Profile = -> Sketch010
  ReferenceAxis = -> Sketch010 [N_Axis]
  Refine = true
  Suppressed = false
  Type = 0
FEATURE [PartDesign::Chamfer] Chamfer003
  Angle = 45
  Base = -> Pad004 [Edge130,Edge152,Edge158,Edge155]
  BaseFeature = -> Pad004
  ChamferType = 0
  FlipDirection = false
  Refine = true
  Size = 3.99
  Size2 = 1
  SupportTransform = false
  Suppressed = false
  UseAllEdges = false
FEATURE [PartDesign::Body] Body  label="power-supply-bracket-body"
  AllowCompound = false
  Group = -> [Sketch,Pad,Sketch001,Pad001,Fillet,Sketch004,Sketch005,Chamfer,Sketch006,Hole,Sketch007,Hole001,Chamfer001,Chamfer002,Sketch008,Pad002,Sketch009,Pad003,Sketch010,Pad004,Chamfer003]
  Origin = -> Origin
  Tip = -> Chamfer003
FEATURE [App::Part] Part  label="power-supply-bracket-part"
  Group = -> [Body]
  Origin = -> Origin001
COMPONENT P37 — same part as P36; its construction recipe is shown at P36.
COMPONENT P38 — recipe-attached ("smc100c-bracket-part", a linked part whose construction recipe lives in a companion FreeCAD document of the same project; that document's serialized recipe follows).
Construction recipe (the companion document, serialized — sketch geometry with constraints, then the solid features built on it; lengths are millimeters unless a unit is written):

FCSTD DOCUMENT  (FreeCAD 1.0R39319 (Git))
Label: smc100c-bracket
License: All rights reserved
objects: PartDesign::Chamfer×6, Sketcher::SketchObject×5, PartDesign::Pad×3, PartDesign::Pocket×1, PartDesign::Body×1, App::Part×1
note: 41 computed .brp shape members not serialized (recipe doc carries the construction recipe); baked Part::Feature solids carry a one-line shape summary decoded from their .brp

FEATURE [Sketcher::SketchObject] Sketch
  ArcFitTolerance = 1e-06
  AttachmentSupport = -> [XZ_Plane]
  FullyConstrained = true
  MakeInternals = false
  MapMode = 5
  Placement = pos=(0,0,0) rot=(1,0,0;1.5708rad)
  sketch-geometry (62):
    g0: LineSegment [constr] StartX=0 StartY=0 StartZ=0 EndX=0 EndY=-5 EndZ=0
    g1: LineSegment [constr] StartX=0 StartY=-5 StartZ=0 EndX=5 EndY=-5 EndZ=0
    g2: LineSegment [constr] StartX=5 StartY=-5 StartZ=0 EndX=5 EndY=0 EndZ=0
    g3: LineSegment [constr] StartX=5 StartY=0 StartZ=0 EndX=0 EndY=0 EndZ=0
    g4: LineSegment [constr] StartX=5 StartY=-5 StartZ=0 EndX=5 EndY=-153 EndZ=0
    g5: LineSegment [constr] StartX=5 StartY=-153 StartZ=0 EndX=174 EndY=-153 EndZ=0
    g6: LineSegment [constr] StartX=174 StartY=-153 StartZ=0 EndX=174 EndY=-5 EndZ=0
    g7: LineSegment [constr] StartX=174 StartY=-5 StartZ=0 EndX=5 EndY=-5 EndZ=0
    g8: Circle CenterX=89.5 CenterY=-79 CenterZ=0 NormalX=0 NormalY=0 NormalZ=1 AngleXU=0 Radius=2.6
    g9: LineSegment StartX=0 StartY=0 StartZ=0 EndX=0 EndY=-158 EndZ=0
    g10: LineSegment StartX=0 StartY=-158 StartZ=0 EndX=179 EndY=-158 EndZ=0
    g11: LineSegment StartX=179 StartY=-158 StartZ=0 EndX=179 EndY=0 EndZ=0
    g12: LineSegment StartX=179 StartY=0 StartZ=0 EndX=0 EndY=0 EndZ=0
    g13: LineSegment [constr] StartX=0 StartY=0 StartZ=0 EndX=0 EndY=-16 EndZ=0
    g14: LineSegment [constr] StartX=0 StartY=-16 StartZ=0 EndX=16 EndY=-16 EndZ=0
    g15: LineSegment [constr] StartX=16 StartY=-16 StartZ=0 EndX=16 EndY=0 EndZ=0
    g16: LineSegment [constr] StartX=16 StartY=0 StartZ=0 EndX=0 EndY=0 EndZ=0
    g17: LineSegment [constr] StartX=0 StartY=-158 StartZ=0 EndX=16 EndY=-158 EndZ=0
    g18: LineSegment [constr] StartX=16 StartY=-158 StartZ=0 EndX=16 EndY=-142 EndZ=0
    g19: LineSegment [constr] StartX=16 StartY=-142 StartZ=0 EndX=0 EndY=-142 EndZ=0
    g20: LineSegment [constr] StartX=0 StartY=-142 StartZ=0 EndX=0 EndY=-158 EndZ=0
    g21: LineSegment [constr] StartX=179 StartY=-158 StartZ=0 EndX=179 EndY=-142 EndZ=0
    g22: LineSegment [constr] StartX=179 StartY=-142 StartZ=0 EndX=163 EndY=-142 EndZ=0
    g23: LineSegment [constr] StartX=163 StartY=-142 StartZ=0 EndX=163 EndY=-158 EndZ=0
    g24: LineSegment [constr] StartX=163 StartY=-158 StartZ=0 EndX=179 EndY=-158 EndZ=0
    g25: LineSegment [constr] StartX=179 StartY=0 StartZ=0 EndX=163 EndY=0 EndZ=0
    g26: LineSegment [constr] StartX=163 StartY=0 StartZ=0 EndX=163 EndY=-16 EndZ=0
    g27: LineSegment [constr] StartX=163 StartY=-16 StartZ=0 EndX=179 EndY=-16 EndZ=0
    g28: LineSegment [constr] StartX=179 StartY=-16 StartZ=0 EndX=179 EndY=0 EndZ=0
    g29: LineSegment [constr] StartX=163 StartY=-16 StartZ=0 EndX=151.7 EndY=-16 EndZ=0
    g30: LineSegment [constr] StartX=151.7 StartY=-16 StartZ=0 EndX=151.7 EndY=-27.3 EndZ=0
    g31: LineSegment [constr] StartX=151.7 StartY=-27.3 StartZ=0 EndX=163 EndY=-27.3 EndZ=0
    g32: LineSegment [constr] StartX=163 StartY=-27.3 StartZ=0 EndX=163 EndY=-16 EndZ=0
    g33: LineSegment [constr] StartX=163 StartY=-142 StartZ=0 EndX=163 EndY=-130.7 EndZ=0
    g34: LineSegment [constr] StartX=163 StartY=-130.7 StartZ=0 EndX=151.7 EndY=-130.7 EndZ=0
    g35: LineSegment [constr] StartX=151.7 StartY=-130.7 StartZ=0 EndX=151.7 EndY=-142 EndZ=0
    g36: LineSegment [constr] StartX=151.7 StartY=-142 StartZ=0 EndX=163 EndY=-142 EndZ=0
    g37: LineSegment [constr] StartX=16 StartY=-142 StartZ=0 EndX=27.3 EndY=-142 EndZ=0
    g38: LineSegment [constr] StartX=27.3 StartY=-142 StartZ=0 EndX=27.3 EndY=-130.7 EndZ=0
    g39: LineSegment [constr] StartX=27.3 StartY=-130.7 StartZ=0 EndX=16 EndY=-130.7 EndZ=0
    g40: LineSegment [constr] StartX=16 StartY=-130.7 StartZ=0 EndX=16 EndY=-142 EndZ=0
    g41: LineSegment [constr] StartX=16 StartY=-16 StartZ=0 EndX=16 EndY=-27.3 EndZ=0
    g42: LineSegment [constr] StartX=16 StartY=-27.3 StartZ=0 EndX=27.3 EndY=-27.3 EndZ=0
    g43: LineSegment [constr] StartX=27.3 StartY=-27.3 StartZ=0 EndX=27.3 EndY=-16 EndZ=0
    g44: LineSegment [constr] StartX=27.3 StartY=-16 StartZ=0 EndX=16 EndY=-16 EndZ=0
    g45: LineSegment StartX=16 StartY=-27.3 StartZ=0 EndX=16 EndY=-130.7 EndZ=0
    g46: LineSegment StartX=27.3 StartY=-142 StartZ=0 EndX=151.7 EndY=-142 EndZ=0
    g47: LineSegment StartX=163 StartY=-130.7 StartZ=0 EndX=163 EndY=-27.3 EndZ=0
    g48: LineSegment StartX=151.7 StartY=-16 StartZ=0 EndX=27.3 EndY=-16 EndZ=0
    g49: LineSegment [constr] StartX=78.185 StartY=-90.315 StartZ=0 EndX=100.815 EndY=-90.315 EndZ=0
    g50: LineSegment [constr] StartX=100.815 StartY=-90.315 StartZ=0 EndX=100.815 EndY=-67.685 EndZ=0
    g51: LineSegment [constr] StartX=100.815 StartY=-67.685 StartZ=0 EndX=78.185 EndY=-67.685 EndZ=0
    g52: LineSegment [constr] StartX=78.185 StartY=-67.685 StartZ=0 EndX=78.185 EndY=-90.315 EndZ=0
    g53: GeomPoint [constr] X=89.5 Y=-79 Z=0
    g54: LineSegment StartX=27.3 StartY=-142 StartZ=0 EndX=89.5 EndY=-90.315 EndZ=0
    g55: LineSegment StartX=89.5 StartY=-90.315 StartZ=0 EndX=151.7 EndY=-142 EndZ=0
    g56: LineSegment StartX=163 StartY=-130.7 StartZ=0 EndX=100.815 EndY=-79 EndZ=0
    g57: LineSegment StartX=100.815 StartY=-79 StartZ=0 EndX=163 EndY=-27.3 EndZ=0
    g58: LineSegment StartX=151.7 StartY=-16 StartZ=0 EndX=89.5 EndY=-67.685 EndZ=0
    g59: LineSegment StartX=89.5 StartY=-67.685 StartZ=0 EndX=27.3 EndY=-16 EndZ=0
    g60: LineSegment StartX=16 StartY=-27.3 StartZ=0 EndX=78.185 EndY=-79 EndZ=0
    g61: LineSegment StartX=78.185 StartY=-79 StartZ=0 EndX=16 EndY=-130.7 EndZ=0
  constraints (159):
    c: Coincident(g0,g1)
    c: Coincident(g1,g2)
    c: Coincident(g2,g3)
    c: Coincident(g3,g0)
    c: Vertical(g0)
    c: Vertical(g2)
    c: Horizontal(g1)
    c: Horizontal(g3)
    c: Distance(g0,g2) = 5
    c: Distance(g1,g3) = 5
    c: Coincident(g0,g-1)
    c: Coincident(g4,g5)
    c: Coincident(g5,g6)
    c: Coincident(g6,g7)
    c: Coincident(g7,g4)
    c: Vertical(g4)
    c: Vertical(g6)
    c: Horizontal(g5)
    c: Horizontal(g7)
    c: Distance(g4,g6) = 169
    c: Distance(g5,g7) = 148
    c: Coincident(g4,g1)
    c: Diameter(g8) = 5.2
    c: Symmetric(g6,g4,g8)
    c: Distance(g9) = 158
    c: Coincident(g9,g0)
    c: PointOnObject(g9,g-2)
    c: Distance(g10) = 179
    c: Coincident(g10,g9)
    c: Horizontal(g10)
    c: Coincident(g11,g10)
    c: PointOnObject(g11,g-1)
    c: Vertical(g11)
    c: Coincident(g12,g11)
    c: Coincident(g12,g0)
    c: Coincident(g13,g14)
    c: Coincident(g14,g15)
    c: Coincident(g15,g16)
    c: Coincident(g16,g13)
    c: Vertical(g13)
    c: Vertical(g15)
    c: Horizontal(g14)
    c: Horizontal(g16)
    c: Distance(g13,g15) = 16
    c: Distance(g14,g16) = 16
    c: Coincident(g13,g0)
    c: Coincident(g17,g18)
    c: Coincident(g18,g19)
    c: Coincident(g19,g20)
    c: Coincident(g20,g17)
    c: Horizontal(g17)
    c: Horizontal(g19)
    c: Vertical(g18)
    c: Vertical(g20)
    c: Distance(g18,g20) = 16
    c: Distance(g17,g19) = 16
    c: Coincident(g17,g9)
    c: Coincident(g21,g22)
    c: Coincident(g22,g23)
    c: Coincident(g23,g24)
    c: Coincident(g24,g21)
    c: Vertical(g21)
    c: Vertical(g23)
    c: Horizontal(g22)
    c: Horizontal(g24)
    c: Distance(g21,g23) = 16
    c: Distance(g22,g24) = 16
    c: Coincident(g21,g10)
    c: Coincident(g25,g26)
    c: Coincident(g26,g27)
    c: Coincident(g27,g28)
    c: Coincident(g28,g25)
    c: Horizontal(g25)
    c: Horizontal(g27)
    c: Vertical(g26)
    c: Vertical(g28)
    c: Distance(g26,g28) = 16
    c: Distance(g25,g27) = 16
    c: Coincident(g25,g11)
    c: Coincident(g29,g30)
    c: Coincident(g30,g31)
    c: Coincident(g31,g32)
    c: Coincident(g32,g29)
    c: Horizontal(g29)
    c: Horizontal(g31)
    c: Vertical(g30)
    c: Vertical(g32)
    c: Distance(g30,g32) = 11.3
    c: Distance(g29,g31) = 11.3
    c: Coincident(g29,g26)
    c: Coincident(g33,g34)
    c: Coincident(g34,g35)
    c: Coincident(g35,g36)
    c: Coincident(g36,g33)
    c: Vertical(g33)
    c: Vertical(g35)
    c: Horizontal(g34)
    c: Horizontal(g36)
    c: Distance(g33,g35) = 11.3
    c: Distance(g34,g36) = 11.3
    c: Coincident(g33,g22)
    c: Coincident(g37,g38)
    c: Coincident(g38,g39)
    c: Coincident(g39,g40)
    c: Coincident(g40,g37)
    c: Horizontal(g37)
    c: Horizontal(g39)
    c: Vertical(g38)
    c: Vertical(g40)
    c: Distance(g38,g40) = 11.3
    c: Distance(g37,g39) = 11.3
    c: Coincident(g37,g18)
    c: Coincident(g41,g42)
    c: Coincident(g42,g43)
    c: Coincident(g43,g44)
    c: Coincident(g44,g41)
    c: Vertical(g41)
    c: Vertical(g43)
    c: Horizontal(g42)
    c: Horizontal(g44)
    c: Distance(g41,g43) = 11.3
    c: Distance(g42,g44) = 11.3
    c: Coincident(g41,g14)
    c: Coincident(g45,g41)
    c: Coincident(g45,g39)
    c: Coincident(g46,g37)
    c: Coincident(g46,g35)
    c: Coincident(g47,g33)
    c: Coincident(g47,g31)
    c: Coincident(g48,g29)
    c: Coincident(g48,g43)
    c: Coincident(g49,g50)
    c: Coincident(g50,g51)
    c: Coincident(g51,g52)
    c: Coincident(g52,g49)
    c: Horizontal(g49)
    c: Horizontal(g51)
    c: Vertical(g50)
    c: Vertical(g52)
    c: Symmetric(g51,g49,g53)
    c: Distance(g50,g52) = 22.63
    c: Distance(g49,g51) = 22.63
    c: Coincident(g53,g8)
    c: Coincident(g54,g37)
    c: Symmetric(g49,g49,g54)
    c: Coincident(g55,g54)
    c: Coincident(g55,g35)
    c: Coincident(g56,g33)
    c: Symmetric(g50,g50,g56)
    c: Coincident(g57,g56)
    c: Coincident(g57,g31)
    c: Coincident(g58,g29)
    c: Symmetric(g51,g51,g58)
    c: Coincident(g59,g58)
    c: Coincident(g59,g43)
    c: Coincident(g60,g41)
    c: Symmetric(g52,g52,g60)
    c: Coincident(g61,g60)
    c: Coincident(g61,g39)
FEATURE [PartDesign::Pad] Pad
  Direction = (0,-1,2e-16)
  Length = 6
  Length2 = 10
  Placement = pos=(0,0,0) rot=(1,0,0;1.5708rad)
  Profile = -> Sketch
  ReferenceAxis = -> Sketch [N_Axis]
  Refine = true
  Reversed = true
  Suppressed = false
  Type = 0
FEATURE [Sketcher::SketchObject] Sketch001
  ArcFitTolerance = 1e-06
  AttachmentSupport = -> [Pad]
  FullyConstrained = true
  MakeInternals = false
  MapMode = 5
  Placement = pos=(179,0,0) rot=(0.707107,0,0.707107;3.14159rad)
  sketch-geometry (4):
    g0: LineSegment StartX=0 StartY=0 StartZ=0 EndX=-5 EndY=0 EndZ=0
    g1: LineSegment StartX=-5 StartY=0 StartZ=0 EndX=-5 EndY=-30 EndZ=0
    g2: LineSegment StartX=-5 StartY=-30 StartZ=0 EndX=0 EndY=-30 EndZ=0
    g3: LineSegment StartX=0 StartY=-30 StartZ=0 EndX=0 EndY=0 EndZ=0
  constraints (11):
    c: Coincident(g0,g1)
    c: Coincident(g1,g2)
    c: Coincident(g2,g3)
    c: Coincident(g3,g0)
    c: Horizontal(g0)
    c: Horizontal(g2)
    c: Vertical(g1)
    c: Vertical(g3)
    c: Distance(g1,g3) = 5
    c: Distance(g0,g2) = 30
    c: Coincident(g0,g-1)
FEATURE [PartDesign::Pad] Pad001
  BaseFeature = -> Pad
  Direction = (1,0,-2e-16)
  Length = 30
  Length2 = 10
  Placement = pos=(0,0,0) rot=(1,0,0;1.5708rad)
  Profile = -> Sketch001
  ReferenceAxis = -> Sketch001 [N_Axis]
  Refine = true
  Suppressed = false
  Type = 0
FEATURE [Sketcher::SketchObject] Sketch002
  ArcFitTolerance = 1e-06
  AttachmentSupport = -> [Pad001]
  FullyConstrained = true
  MakeInternals = false
  MapMode = 5
  Placement = pos=(0,6,0) rot=(-1,0,0;1.5708rad)
  sketch-geometry (5):
    g0: LineSegment [constr] StartX=0 StartY=0 StartZ=0 EndX=174 EndY=0 EndZ=0
    g1: LineSegment StartX=174 StartY=0 StartZ=0 EndX=179 EndY=0 EndZ=0
    g2: LineSegment StartX=179 StartY=0 StartZ=0 EndX=179 EndY=35 EndZ=0
    g3: LineSegment StartX=179 StartY=35 StartZ=0 EndX=174 EndY=35 EndZ=0
    g4: LineSegment StartX=174 StartY=35 StartZ=0 EndX=174 EndY=0 EndZ=0
  constraints (14):
    c: Distance(g0) = 174
    c: Coincident(g0,g-1)
    c: Horizontal(g0)
    c: Coincident(g1,g2)
    c: Coincident(g2,g3)
    c: Coincident(g3,g4)
    c: Coincident(g4,g1)
    c: Horizontal(g1)
    c: Horizontal(g3)
    c: Vertical(g2)
    c: Vertical(g4)
    c: Distance(g2,g4) = 5
    c: Distance(g1,g3) = 35
    c: Coincident(g1,g0)
FEATURE [PartDesign::Pad] Pad002
  BaseFeature = -> Pad001
  Direction = (0,1,2e-16)
  Length = 24
  Length2 = 10
  Placement = pos=(0,0,0) rot=(1,0,0;1.5708rad)
  Profile = -> Sketch002
  ReferenceAxis = -> Sketch002 [N_Axis]
  Refine = true
  Suppressed = false
  Type = 0
FEATURE [Sketcher::SketchObject] Sketch003
  ArcFitTolerance = 1e-06
  AttachmentSupport = -> [Pad002]
  FullyConstrained = true
  MakeInternals = false
  MapMode = 5
  Placement = pos=(0,0,-7e-16) rot=(0,0,1;3.14159rad)
  sketch-geometry (5):
    g0: LineSegment [constr] StartX=0 StartY=0 StartZ=0 EndX=-194 EndY=0 EndZ=0
    g1: LineSegment [constr] StartX=-194 StartY=0 StartZ=0 EndX=-194 EndY=-15 EndZ=0
    g2: LineSegment [constr] StartX=-194 StartY=-15 StartZ=0 EndX=0 EndY=-15 EndZ=0
    g3: LineSegment [constr] StartX=0 StartY=-15 StartZ=0 EndX=0 EndY=0 EndZ=0
    g4: Circle CenterX=-194 CenterY=-15 CenterZ=0 NormalX=0 NormalY=0 NormalZ=1 AngleXU=0 Radius=2.6
  constraints (13):
    c: Coincident(g0,g1)
    c: Coincident(g1,g2)
    c: Coincident(g2,g3)
    c: Coincident(g3,g0)
    c: Horizontal(g0)
    c: Horizontal(g2)
    c: Vertical(g1)
    c: Vertical(g3)
    c: Distance(g1,g3) = 194
    c: Distance(g0,g2) = 15
    c: Coincident(g0,g-1)
    c: Diameter(g4) = 5.2
    c: Coincident(g4,g1)
FEATURE [PartDesign::Pocket] Pocket
  BaseFeature = -> Pad002
  Direction = (0,0,-1)
  Length = 7
  Length2 = 5
  Placement = pos=(0,0,0) rot=(1,0,0;1.5708rad)
  Profile = -> Sketch003
  ReferenceAxis = -> Sketch003 [N_Axis]
  Refine = true
  Suppressed = false
  Type = 0
FEATURE [PartDesign::Chamfer] Chamfer
  Angle = 45
  Base = -> Pocket [Edge47,Edge16]
  BaseFeature = -> Pocket
  ChamferType = 0
  FlipDirection = false
  Placement = pos=(0,0,0) rot=(1,0,0;1.5708rad)
  Refine = true
  Size = 5
  Size2 = 1
  SupportTransform = false
  Suppressed = false
  UseAllEdges = false
FEATURE [PartDesign::Chamfer] Chamfer001
  Angle = 45
  Base = -> Chamfer [Edge57]
  BaseFeature = -> Chamfer
  ChamferType = 0
  FlipDirection = false
  Placement = pos=(0,0,0) rot=(1,0,0;1.5708rad)
  Refine = true
  Size = 5
  Size2 = 1
  SupportTransform = false
  Suppressed = false
  UseAllEdges = false
FEATURE [PartDesign::Chamfer] Chamfer002
  Angle = 45
  Base = -> Chamfer001 [Edge8]
  BaseFeature = -> Chamfer001
  ChamferType = 0
  FlipDirection = false
  Placement = pos=(0,0,0) rot=(1,0,0;1.5708rad)
  Refine = true
  Size = 5
  Size2 = 1
  SupportTransform = false
  Suppressed = false
  UseAllEdges = false
FEATURE [PartDesign::Chamfer] Chamfer003
  Angle = 45
  Base = -> Chamfer002 [Edge42]
  BaseFeature = -> Chamfer002
  ChamferType = 0
  FlipDirection = false
  Placement = pos=(0,0,0) rot=(1,0,0;1.5708rad)
  Refine = true
  Size = 10
  Size2 = 1
  SupportTransform = false
  Suppressed = false
  UseAllEdges = false
FEATURE [PartDesign::Chamfer] Chamfer004
  Angle = 45
  Base = -> Chamfer003 [Edge34]
  BaseFeature = -> Chamfer003
  ChamferType = 0
  FlipDirection = false
  Placement = pos=(0,0,0) rot=(1,0,0;1.5708rad)
  Refine = true
  Size = 10
  Size2 = 1
  SupportTransform = false
  Suppressed = false
  UseAllEdges = false
FEATURE [PartDesign::Chamfer] Chamfer005
  Angle = 45
  Base = -> Chamfer004 [Edge31]
  BaseFeature = -> Chamfer004
  ChamferType = 0
  FlipDirection = false
  Placement = pos=(0,0,0) rot=(1,0,0;1.5708rad)
  Refine = true
  Size = 10
  Size2 = 1
  SupportTransform = false
  Suppressed = false
  UseAllEdges = false
FEATURE [Sketcher::SketchObject] Sketch004
  ArcFitTolerance = 1e-06
  AttachmentSupport = -> [Chamfer005]
  FullyConstrained = true
  MakeInternals = false
  MapMode = 5
  Placement = pos=(0,6,0) rot=(-1,0,0;1.5708rad)
FEATURE [PartDesign::Body] Body  label="smc100c-bracket-body"
  AllowCompound = false
  Group = -> [Sketch,Pad,Sketch001,Pad001,Sketch002,Pad002,Sketch003,Pocket,Chamfer,Chamfer001,Chamfer002,Chamfer003,Chamfer004,Chamfer005,Sketch004]
  Origin = -> Origin
  Tip = -> Chamfer005
FEATURE [App::Part] Part  label="smc100c-bracket-part"
  Group = -> [Body]
  Origin = -> Origin001
COMPONENT P39 — same part as P38; its construction recipe is shown at P38.
PROVENANCE & LICENSES
A FreeCAD (.FCStd) document from a public repository crawl; recipes are the document's own serialized feature recipes (and, for linked parts, companion documents' recipes).
License: other.
